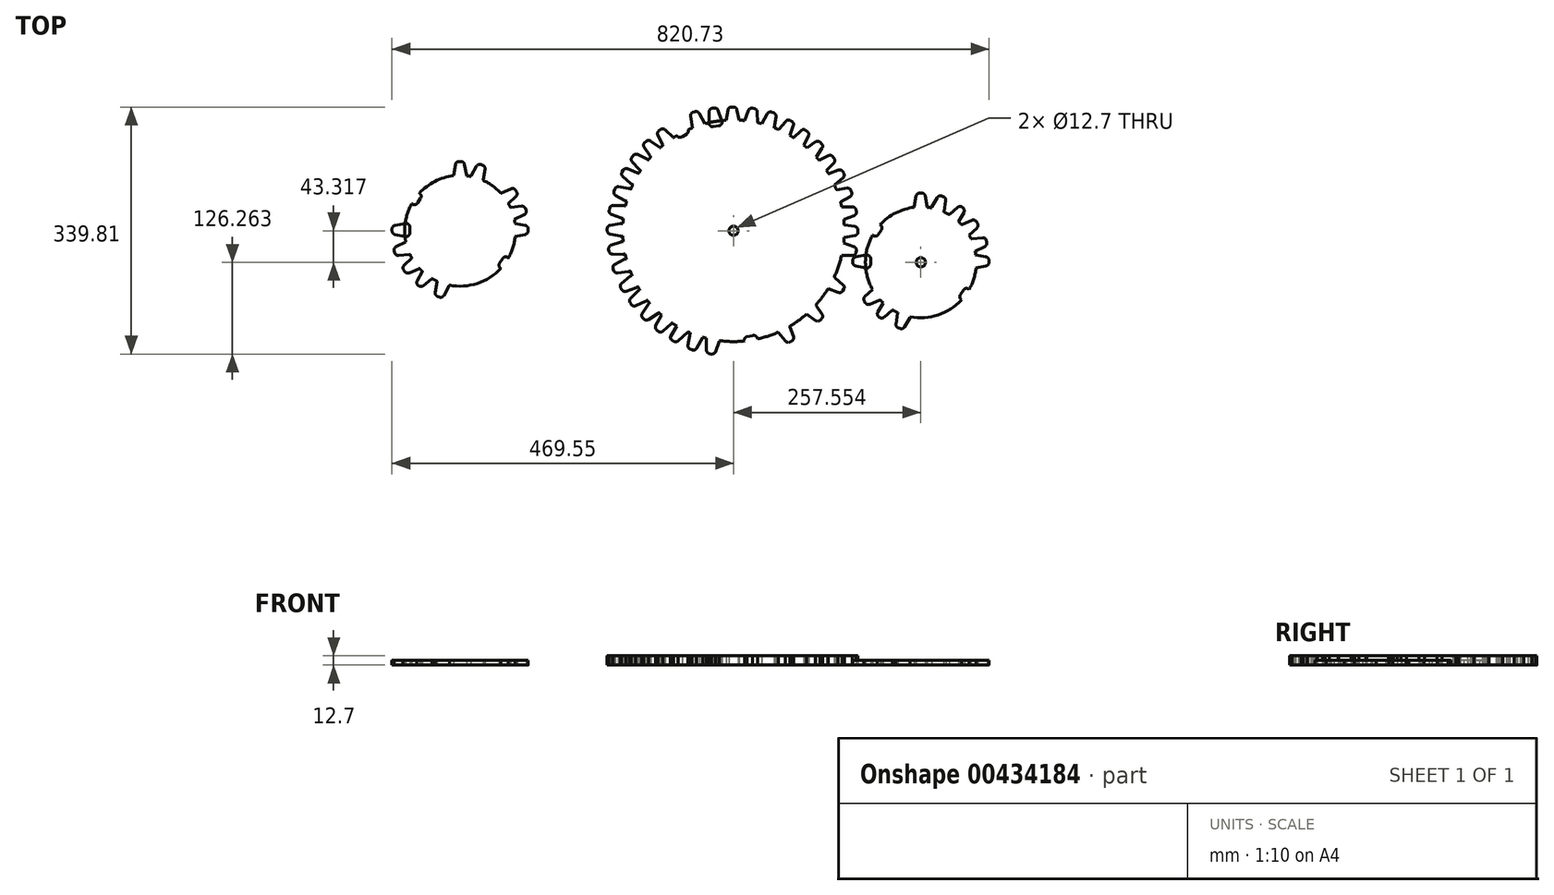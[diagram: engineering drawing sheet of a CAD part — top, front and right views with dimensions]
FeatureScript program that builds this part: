
annotation { "Feature Type Name" : "Feature", "Feature Type Description" : "" }
export const myFeature = defineFeature(function(context is Context, id is Id, definition is map)
    precondition{}
    {
        {
            var Q0;
            Q0=qCreatedBy(makeId("Top.planeOp"),FACE);
            var sketch = newSketch(context, id + "F0", { "sketchPlane" : qUnion([Q0])});
            skCircle(sketch, "E0", {"center": v(0, 0) * mm, "radius": 152.4 * mm});
            skCircle(sketch, "E1", {"center": v(0, 0) * mm, "radius": 6.35 * mm});
            skCircle(sketch, "E2", {"center": v(-375.92, 0) * mm, "radius": 76.2 * mm});
            skCircle(sketch, "E3", {"center": v(-375.92, 0) * mm, "radius": 6.35 * mm});
            skLineSegment(sketch, "E4", {"start": v(-2.72, 170.23) * mm, "end": v(-0.18, 170.23) * mm});
            skLineSegment(sketch, "E5", {"start": v(4.82, 166.07) * mm, "end": v(7.48, 151.67) * mm});
            skLineSegment(sketch, "E6", {"start": v(-7.73, 165.99) * mm, "end": v(-10.15, 151.52) * mm});
            skLineSegment(sketch, "E7", {"start": v(-5.1, 145.6) * mm, "end": v(2.53, 145.66) * mm});
            skPoint(sketch, "E8.visualSharp", {"position": v(-7.01, 170.23) * mm});
            skArc(sketch, "E8.filletArc", {"start": v(-2.72, 170.23) * mm, "mid": v(-6, 169.03) * mm, "end": v(-7.73, 165.99) * mm});
            skPoint(sketch, "E9.visualSharp", {"position": v(4.05, 170.23) * mm});
            skArc(sketch, "E9.filletArc", {"start": v(4.82, 166.07) * mm, "mid": v(3.07, 169.05) * mm, "end": v(-0.18, 170.23) * mm});
            skPoint(sketch, "E10.visualSharp", {"position": v(8.58, 145.71) * mm});
            skArc(sketch, "E10.filletArc", {"start": v(2.53, 145.66) * mm, "mid": v(6.4, 147.51) * mm, "end": v(7.48, 151.67) * mm});
            skPoint(sketch, "E11.visualSharp", {"position": v(-11.16, 145.55) * mm});
            skArc(sketch, "E11.filletArc", {"start": v(-10.15, 151.52) * mm, "mid": v(-9, 147.38) * mm, "end": v(-5.1, 145.6) * mm});
            skLineSegment(sketch, "E12", {"start": v(26.05, 168.6) * mm, "end": v(28.55, 168.15) * mm});
            skLineSegment(sketch, "E13", {"start": v(32.75, 163.19) * mm, "end": v(32.88, 147.84) * mm});
            skLineSegment(sketch, "E14", {"start": v(20.38, 165.29) * mm, "end": v(15.25, 150.8) * mm});
            skLineSegment(sketch, "E15", {"start": v(19.2, 144.1) * mm, "end": v(26.96, 142.79) * mm});
            skArc(sketch, "E16.filletArc", {"start": v(26.05, 168.6) * mm, "mid": v(22.61, 167.98) * mm, "end": v(20.38, 165.29) * mm});
            skArc(sketch, "E17.filletArc", {"start": v(32.75, 163.19) * mm, "mid": v(31.55, 166.43) * mm, "end": v(28.55, 168.15) * mm});
            skArc(sketch, "E18.filletArc", {"start": v(26.96, 142.79) * mm, "mid": v(31.1, 143.94) * mm, "end": v(32.88, 147.84) * mm});
            skArc(sketch, "E19.filletArc", {"start": v(15.25, 150.8) * mm, "mid": v(15.65, 146.53) * mm, "end": v(19.2, 144.1) * mm});
            skLineSegment(sketch, "E20", {"start": v(52.66, 163.16) * mm, "end": v(55.04, 162.3) * mm});
            skLineSegment(sketch, "E21", {"start": v(58.32, 156.68) * mm, "end": v(55.65, 140.78) * mm});
            skLineSegment(sketch, "E22", {"start": v(46.5, 160.9) * mm, "end": v(38.54, 146.85) * mm});
            skLineSegment(sketch, "E23", {"start": v(41.27, 139.56) * mm, "end": v(48.94, 136.83) * mm});
            skArc(sketch, "E24.filletArc", {"start": v(52.66, 163.16) * mm, "mid": v(49.16, 163.16) * mm, "end": v(46.5, 160.9) * mm});
            skArc(sketch, "E25.filletArc", {"start": v(58.32, 156.68) * mm, "mid": v(57.7, 160.08) * mm, "end": v(55.04, 162.3) * mm});
            skArc(sketch, "E26.filletArc", {"start": v(48.94, 136.83) * mm, "mid": v(53.21, 137.24) * mm, "end": v(55.65, 140.78) * mm});
            skArc(sketch, "E27.filletArc", {"start": v(38.54, 146.85) * mm, "mid": v(38.2, 142.57) * mm, "end": v(41.27, 139.56) * mm});
            skLineSegment(sketch, "E28", {"start": v(78, 151.7) * mm, "end": v(79.99, 150.55) * mm});
            skLineSegment(sketch, "E29", {"start": v(82.23, 144.45) * mm, "end": v(77.34, 130.64) * mm});
            skLineSegment(sketch, "E30", {"start": v(71.55, 150.52) * mm, "end": v(62.21, 139.2) * mm});
            skLineSegment(sketch, "E31", {"start": v(63.63, 131.56) * mm, "end": v(70.05, 127.92) * mm});
            skArc(sketch, "E32.filletArc", {"start": v(78, 151.7) * mm, "mid": v(74.56, 152.3) * mm, "end": v(71.55, 150.52) * mm});
            skArc(sketch, "E33.filletArc", {"start": v(82.23, 144.45) * mm, "mid": v(82.21, 147.9) * mm, "end": v(79.99, 150.55) * mm});
            skArc(sketch, "E34.filletArc", {"start": v(70.05, 127.92) * mm, "mid": v(74.33, 127.58) * mm, "end": v(77.34, 130.64) * mm});
            skArc(sketch, "E35.filletArc", {"start": v(62.21, 139.2) * mm, "mid": v(61.13, 135.05) * mm, "end": v(63.63, 131.56) * mm});
            skLineSegment(sketch, "E36", {"start": v(99.42, 138.15) * mm, "end": v(101.44, 136.6) * mm});
            skLineSegment(sketch, "E37", {"start": v(102.88, 130.27) * mm, "end": v(96.23, 117.22) * mm});
            skLineSegment(sketch, "E38", {"start": v(92.87, 137.83) * mm, "end": v(82.14, 127.83) * mm});
            skLineSegment(sketch, "E39", {"start": v(82.55, 120.05) * mm, "end": v(88.65, 115.46) * mm});
            skArc(sketch, "E40.filletArc", {"start": v(99.42, 138.15) * mm, "mid": v(96.09, 139.2) * mm, "end": v(92.87, 137.83) * mm});
            skArc(sketch, "E41.filletArc", {"start": v(102.88, 130.27) * mm, "mid": v(103.3, 133.7) * mm, "end": v(101.44, 136.6) * mm});
            skArc(sketch, "E42.filletArc", {"start": v(88.65, 115.46) * mm, "mid": v(92.85, 114.57) * mm, "end": v(96.23, 117.22) * mm});
            skArc(sketch, "E43.filletArc", {"start": v(82.14, 127.83) * mm, "mid": v(80.53, 123.84) * mm, "end": v(82.55, 120.05) * mm});
            skLineSegment(sketch, "E44", {"start": v(119.21, 121.66) * mm, "end": v(121, 119.87) * mm});
            skLineSegment(sketch, "E45", {"start": v(121.6, 113.4) * mm, "end": v(113.3, 101.33) * mm});
            skLineSegment(sketch, "E46", {"start": v(112.67, 122.2) * mm, "end": v(100.73, 113.7) * mm});
            skLineSegment(sketch, "E47", {"start": v(100.11, 105.94) * mm, "end": v(105.55, 100.58) * mm});
            skArc(sketch, "E48.filletArc", {"start": v(119.21, 121.66) * mm, "mid": v(116.04, 123.13) * mm, "end": v(112.67, 122.2) * mm});
            skArc(sketch, "E49.filletArc", {"start": v(121.6, 113.4) * mm, "mid": v(122.48, 116.74) * mm, "end": v(121, 119.87) * mm});
            skArc(sketch, "E50.filletArc", {"start": v(105.55, 100.58) * mm, "mid": v(109.6, 99.15) * mm, "end": v(113.3, 101.33) * mm});
            skArc(sketch, "E51.filletArc", {"start": v(100.73, 113.7) * mm, "mid": v(98.61, 109.96) * mm, "end": v(100.11, 105.94) * mm});
            skLineSegment(sketch, "E52", {"start": v(136.86, 101.65) * mm, "end": v(138.32, 99.57) * mm});
            skLineSegment(sketch, "E53", {"start": v(137.78, 93.1) * mm, "end": v(127.5, 82.65) * mm});
            skLineSegment(sketch, "E54", {"start": v(130.52, 103.32) * mm, "end": v(117.27, 97.01) * mm});
            skLineSegment(sketch, "E55", {"start": v(115.32, 89.48) * mm, "end": v(119.75, 83.26) * mm});
            skArc(sketch, "E56.filletArc", {"start": v(136.86, 101.65) * mm, "mid": v(134, 103.65) * mm, "end": v(130.52, 103.32) * mm});
            skArc(sketch, "E57.filletArc", {"start": v(137.78, 93.1) * mm, "mid": v(139.22, 96.23) * mm, "end": v(138.32, 99.57) * mm});
            skArc(sketch, "E58.filletArc", {"start": v(119.75, 83.26) * mm, "mid": v(123.49, 81.15) * mm, "end": v(127.5, 82.65) * mm});
            skArc(sketch, "E59.filletArc", {"start": v(117.27, 97.01) * mm, "mid": v(114.54, 93.7) * mm, "end": v(115.32, 89.48) * mm});
            skLineSegment(sketch, "E60", {"start": v(150.3, 81.3) * mm, "end": v(151.56, 79.1) * mm});
            skLineSegment(sketch, "E61", {"start": v(150.46, 72.7) * mm, "end": v(139.32, 63.18) * mm});
            skLineSegment(sketch, "E62", {"start": v(144.12, 83.51) * mm, "end": v(130.37, 78.38) * mm});
            skLineSegment(sketch, "E63", {"start": v(127.77, 71.05) * mm, "end": v(131.64, 64.47) * mm});
            skArc(sketch, "E64.filletArc", {"start": v(150.3, 81.3) * mm, "mid": v(147.61, 83.54) * mm, "end": v(144.12, 83.51) * mm});
            skArc(sketch, "E65.filletArc", {"start": v(150.46, 72.7) * mm, "mid": v(152.17, 75.7) * mm, "end": v(151.56, 79.1) * mm});
            skArc(sketch, "E66.filletArc", {"start": v(131.64, 64.47) * mm, "mid": v(135.18, 62.04) * mm, "end": v(139.32, 63.18) * mm});
            skArc(sketch, "E67.filletArc", {"start": v(130.37, 78.38) * mm, "mid": v(127.36, 75.32) * mm, "end": v(127.77, 71.05) * mm});
            skLineSegment(sketch, "E68", {"start": v(161.65, 55.18) * mm, "end": v(162.43, 52.77) * mm});
            skLineSegment(sketch, "E69", {"start": v(160.02, 46.73) * mm, "end": v(147.14, 39.75) * mm});
            skLineSegment(sketch, "E70", {"start": v(156.07, 58.64) * mm, "end": v(141.56, 56.48) * mm});
            skLineSegment(sketch, "E71", {"start": v(137.48, 49.85) * mm, "end": v(139.9, 42.61) * mm});
            skArc(sketch, "E72.filletArc", {"start": v(161.65, 55.18) * mm, "mid": v(159.49, 57.93) * mm, "end": v(156.07, 58.64) * mm});
            skArc(sketch, "E73.filletArc", {"start": v(160.02, 46.73) * mm, "mid": v(162.31, 49.31) * mm, "end": v(162.43, 52.77) * mm});
            skArc(sketch, "E74.filletArc", {"start": v(139.9, 42.61) * mm, "mid": v(142.85, 39.5) * mm, "end": v(147.14, 39.75) * mm});
            skArc(sketch, "E75.filletArc", {"start": v(141.56, 56.48) * mm, "mid": v(137.97, 54.12) * mm, "end": v(137.48, 49.85) * mm});
            skLineSegment(sketch, "E76", {"start": v(168.33, 28.75) * mm, "end": v(168.77, 26.25) * mm});
            skLineSegment(sketch, "E77", {"start": v(165.55, 20.6) * mm, "end": v(151.82, 15.48) * mm});
            skLineSegment(sketch, "E78", {"start": v(163.29, 32.95) * mm, "end": v(148.62, 32.83) * mm});
            skLineSegment(sketch, "E79", {"start": v(143.66, 26.82) * mm, "end": v(145.05, 19.32) * mm});
            skArc(sketch, "E80.filletArc", {"start": v(168.33, 28.75) * mm, "mid": v(166.58, 31.77) * mm, "end": v(163.29, 32.95) * mm});
            skArc(sketch, "E81.filletArc", {"start": v(165.55, 20.6) * mm, "mid": v(168.18, 22.85) * mm, "end": v(168.77, 26.25) * mm});
            skArc(sketch, "E82.filletArc", {"start": v(145.05, 19.32) * mm, "mid": v(147.54, 15.82) * mm, "end": v(151.82, 15.48) * mm});
            skArc(sketch, "E83.filletArc", {"start": v(148.62, 32.83) * mm, "mid": v(144.74, 30.98) * mm, "end": v(143.66, 26.82) * mm});
            skLineSegment(sketch, "E84", {"start": v(171.1, 0.88) * mm, "end": v(171.1, -1.66) * mm});
            skLineSegment(sketch, "E85", {"start": v(166.93, -6.65) * mm, "end": v(152.53, -9.31) * mm});
            skLineSegment(sketch, "E86", {"start": v(166.85, 5.9) * mm, "end": v(152.38, 8.32) * mm});
            skLineSegment(sketch, "E87", {"start": v(146.46, 3.27) * mm, "end": v(146.53, -4.36) * mm});
            skArc(sketch, "E88.filletArc", {"start": v(171.1, 0.88) * mm, "mid": v(169.89, 4.17) * mm, "end": v(166.85, 5.9) * mm});
            skArc(sketch, "E89.filletArc", {"start": v(166.93, -6.65) * mm, "mid": v(169.92, -4.9) * mm, "end": v(171.1, -1.66) * mm});
            skArc(sketch, "E90.filletArc", {"start": v(146.53, -4.36) * mm, "mid": v(148.37, -8.24) * mm, "end": v(152.53, -9.31) * mm});
            skArc(sketch, "E91.filletArc", {"start": v(152.38, 8.32) * mm, "mid": v(148.25, 7.18) * mm, "end": v(146.46, 3.27) * mm});
            skArc(sketch, "E92.MirrorCS", {"start": v(32.75, -164.43) * mm, "mid": v(31.55, -167.65) * mm, "end": v(28.57, -169.36) * mm});
            skLineSegment(sketch, "E93.MirrorCS", {"start": v(26.07, -169.8) * mm, "end": v(28.57, -169.36) * mm});
            skArc(sketch, "E94.MirrorCS", {"start": v(81.8, -128.72) * mm, "mid": v(80.51, -125.06) * mm, "end": v(82.17, -121.56) * mm});
            skArc(sketch, "E95.MirrorCS", {"start": v(15.04, -151.45) * mm, "mid": v(15.62, -147.73) * mm, "end": v(18.6, -145.4) * mm});
            skLineSegment(sketch, "E96.MirrorCS", {"start": v(18.6, -145.4) * mm, "end": v(26.36, -144.1) * mm});
            skArc(sketch, "E97.MirrorCS", {"start": v(26.36, -144.1) * mm, "mid": v(30.63, -144.76) * mm, "end": v(32.88, -148.45) * mm});
            skLineSegment(sketch, "E98.MirrorCS", {"start": v(82.17, -121.56) * mm, "end": v(88.88, -116.5) * mm});
            skLineSegment(sketch, "E99.MirrorCS", {"start": v(168.32, -30.06) * mm, "end": v(168.87, -26.9) * mm});
            skArc(sketch, "E100.MirrorCS", {"start": v(99.04, -139.66) * mm, "mid": v(95.6, -140.39) * mm, "end": v(92.52, -138.72) * mm});
            skLineSegment(sketch, "E101.MirrorCS", {"start": v(63.17, -133.03) * mm, "end": v(70.24, -129.03) * mm});
            skArc(sketch, "E102.MirrorCS", {"start": v(165, -21.62) * mm, "mid": v(167.89, -23.55) * mm, "end": v(168.87, -26.9) * mm});
            skArc(sketch, "E103.MirrorCS", {"start": v(141.38, -57.68) * mm, "mid": v(137.97, -55.34) * mm, "end": v(137.43, -51.23) * mm});
            skArc(sketch, "E104.MirrorCS", {"start": v(4.8, -167.37) * mm, "mid": v(3, -170.32) * mm, "end": v(-0.26, -171.44) * mm});
            skArc(sketch, "E105.MirrorCS", {"start": v(26.07, -169.8) * mm, "mid": v(22.63, -169.2) * mm, "end": v(20.39, -166.52) * mm});
            skArc(sketch, "E106.MirrorCS", {"start": v(131.88, -65.27) * mm, "mid": v(135.65, -63.18) * mm, "end": v(139.68, -64.71) * mm});
            skArc(sketch, "E107.MirrorCS", {"start": v(168.32, -30.06) * mm, "mid": v(166.5, -33.05) * mm, "end": v(163.2, -34.16) * mm});
            skArc(sketch, "E108.MirrorCS", {"start": v(-10.25, -152.13) * mm, "mid": v(-9.04, -148.58) * mm, "end": v(-5.72, -146.81) * mm});
            skArc(sketch, "E109.MirrorCS", {"start": v(70.24, -129.03) * mm, "mid": v(74.54, -128.88) * mm, "end": v(77.41, -132.07) * mm});
            skLineSegment(sketch, "E110.MirrorCS", {"start": v(118.91, -123.18) * mm, "end": v(121.27, -120.82) * mm});
            skLineSegment(sketch, "E111.MirrorCS", {"start": v(-3.33, -171.44) * mm, "end": v(-0.26, -171.44) * mm});
            skArc(sketch, "E112.MirrorCS", {"start": v(-3.33, -171.44) * mm, "mid": v(-6.47, -169.85) * mm, "end": v(-7.83, -166.6) * mm});
            skArc(sketch, "E113.MirrorCS", {"start": v(1.95, -146.88) * mm, "mid": v(6.03, -148.28) * mm, "end": v(7.59, -152.31) * mm});
            skLineSegment(sketch, "E114.MirrorCS", {"start": v(-5.72, -146.81) * mm, "end": v(1.95, -146.88) * mm});
            skArc(sketch, "E115.MirrorCS", {"start": v(118.91, -123.18) * mm, "mid": v(115.62, -124.38) * mm, "end": v(112.33, -123.18) * mm});
            skArc(sketch, "E116.MirrorCS", {"start": v(120, -84.12) * mm, "mid": v(123.93, -82.33) * mm, "end": v(127.82, -84.18) * mm});
            skArc(sketch, "E117.MirrorCS", {"start": v(116.97, -98.08) * mm, "mid": v(114.53, -94.92) * mm, "end": v(115.13, -90.97) * mm});
            skArc(sketch, "E118.MirrorCS", {"start": v(138.1, -94.63) * mm, "mid": v(139.24, -97.45) * mm, "end": v(138.58, -100.42) * mm});
            skArc(sketch, "E119.MirrorCS", {"start": v(58.34, -158.02) * mm, "mid": v(57.7, -161.3) * mm, "end": v(55.16, -163.47) * mm});
            skLineSegment(sketch, "E120.MirrorCS", {"start": v(99.81, -107.45) * mm, "end": v(105.81, -101.55) * mm});
            skLineSegment(sketch, "E121.MirrorCS", {"start": v(121.81, -114.91) * mm, "end": v(113.5, -102.84) * mm});
            skLineSegment(sketch, "E122.MirrorCS", {"start": v(165, -21.62) * mm, "end": v(151.28, -16.5) * mm});
            skLineSegment(sketch, "E123.MirrorCS", {"start": v(115.13, -90.97) * mm, "end": v(120, -84.12) * mm});
            skLineSegment(sketch, "E124.MirrorCS", {"start": v(40.73, -140.96) * mm, "end": v(48.36, -138.26) * mm});
            skArc(sketch, "E125.MirrorCS", {"start": v(48.36, -138.26) * mm, "mid": v(52.68, -138.15) * mm, "end": v(55.55, -141.4) * mm});
            skArc(sketch, "E126.MirrorCS", {"start": v(88.88, -116.5) * mm, "mid": v(93.14, -115.86) * mm, "end": v(96.36, -118.7) * mm});
            skArc(sketch, "E127.MirrorCS", {"start": v(140.07, -43.3) * mm, "mid": v(143.36, -40.51) * mm, "end": v(147.62, -41.23) * mm});
            skArc(sketch, "E128.MirrorCS", {"start": v(52.12, -164.58) * mm, "mid": v(48.63, -164.17) * mm, "end": v(46.22, -161.61) * mm});
            skLineSegment(sketch, "E129.MirrorCS", {"start": v(150.15, -82.77) * mm, "end": v(151.8, -79.9) * mm});
            skLineSegment(sketch, "E130.MirrorCS", {"start": v(77.55, -153.17) * mm, "end": v(80.18, -151.65) * mm});
            skLineSegment(sketch, "E131.MirrorCS", {"start": v(92.52, -138.72) * mm, "end": v(81.8, -128.72) * mm});
            skLineSegment(sketch, "E132.MirrorCS", {"start": v(71.21, -151.34) * mm, "end": v(61.88, -140.02) * mm});
            skArc(sketch, "E133.MirrorCS", {"start": v(38.26, -147.57) * mm, "mid": v(38.17, -143.77) * mm, "end": v(40.73, -140.96) * mm});
            skArc(sketch, "E134.MirrorCS", {"start": v(159.53, -47.69) * mm, "mid": v(162.1, -50.02) * mm, "end": v(162.6, -53.46) * mm});
            skArc(sketch, "E135.MirrorCS", {"start": v(103.01, -131.75) * mm, "mid": v(103.31, -134.92) * mm, "end": v(101.68, -137.64) * mm});
            skLineSegment(sketch, "E136.MirrorCS", {"start": v(20.39, -166.52) * mm, "end": v(15.04, -151.45) * mm});
            skLineSegment(sketch, "E137.MirrorCS", {"start": v(137.43, -51.23) * mm, "end": v(140.07, -43.3) * mm});
            skLineSegment(sketch, "E138.MirrorCS", {"start": v(143.65, -28.13) * mm, "end": v(145.16, -19.96) * mm});
            skArc(sketch, "E139.MirrorCS", {"start": v(100.38, -114.67) * mm, "mid": v(98.6, -111.18) * mm, "end": v(99.81, -107.45) * mm});
            skLineSegment(sketch, "E140.MirrorCS", {"start": v(130.21, -104.39) * mm, "end": v(116.97, -98.08) * mm});
            skArc(sketch, "E141.MirrorCS", {"start": v(145.16, -19.96) * mm, "mid": v(147.53, -17.01) * mm, "end": v(151.28, -16.5) * mm});
            skArc(sketch, "E142.MirrorCS", {"start": v(105.81, -101.55) * mm, "mid": v(109.96, -100.4) * mm, "end": v(113.5, -102.84) * mm});
            skArc(sketch, "E143.MirrorCS", {"start": v(161.6, -56.57) * mm, "mid": v(159.34, -59.24) * mm, "end": v(155.9, -59.83) * mm});
            skArc(sketch, "E144.MirrorCS", {"start": v(121.81, -114.91) * mm, "mid": v(122.49, -117.96) * mm, "end": v(121.27, -120.82) * mm});
            skLineSegment(sketch, "E145.MirrorCS", {"start": v(138.1, -94.63) * mm, "end": v(127.82, -84.18) * mm});
            skArc(sketch, "E146.MirrorCS", {"start": v(82.31, -145.88) * mm, "mid": v(82.22, -149.12) * mm, "end": v(80.18, -151.65) * mm});
            skLineSegment(sketch, "E147.MirrorCS", {"start": v(161.6, -56.57) * mm, "end": v(162.6, -53.46) * mm});
            skArc(sketch, "E148.MirrorCS", {"start": v(130.1, -79.5) * mm, "mid": v(127.35, -76.54) * mm, "end": v(127.62, -72.52) * mm});
            skArc(sketch, "E149.MirrorCS", {"start": v(136.67, -103.14) * mm, "mid": v(133.67, -104.95) * mm, "end": v(130.21, -104.39) * mm});
            skLineSegment(sketch, "E150.MirrorCS", {"start": v(159.53, -47.69) * mm, "end": v(147.62, -41.23) * mm});
            skLineSegment(sketch, "E151.MirrorCS", {"start": v(155.9, -59.83) * mm, "end": v(141.38, -57.68) * mm});
            skLineSegment(sketch, "E152.MirrorCS", {"start": v(103.01, -131.75) * mm, "end": v(96.36, -118.7) * mm});
            skLineSegment(sketch, "E153.MirrorCS", {"start": v(143.84, -84.63) * mm, "end": v(130.1, -79.5) * mm});
            skLineSegment(sketch, "E154.MirrorCS", {"start": v(136.67, -103.14) * mm, "end": v(138.58, -100.42) * mm});
            skLineSegment(sketch, "E155.MirrorCS", {"start": v(150.83, -74.22) * mm, "end": v(139.68, -64.71) * mm});
            skArc(sketch, "E156.MirrorCS", {"start": v(150.83, -74.22) * mm, "mid": v(152.2, -76.9) * mm, "end": v(151.8, -79.9) * mm});
            skLineSegment(sketch, "E157.MirrorCS", {"start": v(82.31, -145.88) * mm, "end": v(77.41, -132.07) * mm});
            skLineSegment(sketch, "E158.MirrorCS", {"start": v(52.12, -164.58) * mm, "end": v(55.16, -163.47) * mm});
            skArc(sketch, "E159.MirrorCS", {"start": v(61.88, -140.02) * mm, "mid": v(61.1, -136.26) * mm, "end": v(63.17, -133.03) * mm});
            skLineSegment(sketch, "E160.MirrorCS", {"start": v(99.04, -139.66) * mm, "end": v(101.68, -137.64) * mm});
            skLineSegment(sketch, "E161.MirrorCS", {"start": v(112.33, -123.18) * mm, "end": v(100.38, -114.67) * mm});
            skArc(sketch, "E162.MirrorCS", {"start": v(77.55, -153.17) * mm, "mid": v(74.05, -153.41) * mm, "end": v(71.21, -151.34) * mm});
            skArc(sketch, "E163.MirrorCS", {"start": v(150.15, -82.77) * mm, "mid": v(147.33, -84.85) * mm, "end": v(143.84, -84.63) * mm});
            skLineSegment(sketch, "E164.MirrorCS", {"start": v(127.62, -72.52) * mm, "end": v(131.88, -65.27) * mm});
            skArc(sketch, "E165.MirrorCS", {"start": v(148.53, -34.04) * mm, "mid": v(144.74, -32.2) * mm, "end": v(143.65, -28.13) * mm});
            skLineSegment(sketch, "E166.MirrorCS", {"start": v(163.2, -34.16) * mm, "end": v(148.53, -34.04) * mm});
            skLineSegment(sketch, "E167.MirrorCS", {"start": v(46.22, -161.61) * mm, "end": v(38.26, -147.57) * mm});
            skLineSegment(sketch, "E168.MirrorCS", {"start": v(58.34, -158.02) * mm, "end": v(55.55, -141.4) * mm});
            skLineSegment(sketch, "E169.MirrorCS", {"start": v(4.8, -167.37) * mm, "end": v(7.59, -152.31) * mm});
            skLineSegment(sketch, "E170.MirrorCS", {"start": v(32.75, -164.43) * mm, "end": v(32.88, -148.45) * mm});
            skPoint(sketch, "E171.MirrorP", {"position": v(-11.16, -146.77) * mm});
            skPoint(sketch, "E172.MirrorP", {"position": v(8.58, -146.93) * mm});
            skLineSegment(sketch, "E173.MirrorCS", {"start": v(-7.83, -166.6) * mm, "end": v(-10.25, -152.13) * mm});
            skLineSegment(sketch, "E174.MirrorCS", {"start": v(-173.6, 3.46) * mm, "end": v(-173.64, 0.11) * mm});
            skArc(sketch, "E175.MirrorCS", {"start": v(-82.62, -151.8) * mm, "mid": v(-79.23, -152.7) * mm, "end": v(-76.06, -151.2) * mm});
            skArc(sketch, "E176.MirrorCS", {"start": v(-103.9, -137.94) * mm, "mid": v(-100.67, -139.3) * mm, "end": v(-97.32, -138.26) * mm});
            skArc(sketch, "E177.MirrorCS", {"start": v(-86.57, -145.06) * mm, "mid": v(-86.46, -148.16) * mm, "end": v(-84.59, -150.63) * mm});
            skLineSegment(sketch, "E178.MirrorCS", {"start": v(-163.37, 57.56) * mm, "end": v(-164.47, 54.28) * mm});
            skArc(sketch, "E179.MirrorCS", {"start": v(-107.12, -130.68) * mm, "mid": v(-107.4, -133.72) * mm, "end": v(-105.9, -136.37) * mm});
            skLineSegment(sketch, "E180.MirrorCS", {"start": v(-137.97, 103.58) * mm, "end": v(-140, 100.75) * mm});
            skArc(sketch, "E181.MirrorCS", {"start": v(-173.6, 3.46) * mm, "mid": v(-172.4, 6.14) * mm, "end": v(-169.91, 7.72) * mm});
            skArc(sketch, "E182.MirrorCS", {"start": v(-147.42, 20.7) * mm, "mid": v(-150.15, 17.38) * mm, "end": v(-154.45, 17.34) * mm});
            skLineSegment(sketch, "E183.MirrorCS", {"start": v(-103.9, -137.94) * mm, "end": v(-105.9, -136.37) * mm});
            skArc(sketch, "E184.MirrorCS", {"start": v(-139.6, 95.03) * mm, "mid": v(-140.68, 97.83) * mm, "end": v(-140, 100.75) * mm});
            skArc(sketch, "E185.MirrorCS", {"start": v(-149.1, -2.87) * mm, "mid": v(-151.15, -6.65) * mm, "end": v(-155.36, -7.52) * mm});
            skLineSegment(sketch, "E186.MirrorCS", {"start": v(-78.61, 152.7) * mm, "end": v(-81.33, 151.17) * mm});
            skArc(sketch, "E187.MirrorCS", {"start": v(-163.37, 57.56) * mm, "mid": v(-161.37, 59.8) * mm, "end": v(-158.47, 60.52) * mm});
            skArc(sketch, "E188.MirrorCS", {"start": v(-137.97, 103.58) * mm, "mid": v(-135.35, 105.2) * mm, "end": v(-132.27, 105.01) * mm});
            skArc(sketch, "E189.MirrorCS", {"start": v(-78.61, 152.7) * mm, "mid": v(-75.14, 153.1) * mm, "end": v(-72.22, 151.17) * mm});
            skLineSegment(sketch, "E190.MirrorCS", {"start": v(-151.65, 83.43) * mm, "end": v(-153.42, 80.44) * mm});
            skArc(sketch, "E191.MirrorCS", {"start": v(-83.31, 145.96) * mm, "mid": v(-83.1, 148.86) * mm, "end": v(-81.33, 151.17) * mm});
            skLineSegment(sketch, "E192.MirrorCS", {"start": v(-82.62, -151.8) * mm, "end": v(-84.59, -150.63) * mm});
            skArc(sketch, "E193.MirrorCS", {"start": v(-27.85, 143.1) * mm, "mid": v(-31.98, 144.3) * mm, "end": v(-33.72, 148.22) * mm});
            skArc(sketch, "E194.MirrorCS", {"start": v(-169.74, -4.69) * mm, "mid": v(-172.5, -2.95) * mm, "end": v(-173.64, 0.11) * mm});
            skLineSegment(sketch, "E195.MirrorCS", {"start": v(-123.15, 115.25) * mm, "end": v(-114.98, 103.09) * mm});
            skArc(sketch, "E196.MirrorCS", {"start": v(-152.5, 74.73) * mm, "mid": v(-153.85, 77.44) * mm, "end": v(-153.42, 80.44) * mm});
            skLineSegment(sketch, "E197.MirrorCS", {"start": v(-83.31, 145.96) * mm, "end": v(-78.3, 131.32) * mm});
            skArc(sketch, "E198.MirrorCS", {"start": v(-101.67, 114.64) * mm, "mid": v(-99.87, 111.1) * mm, "end": v(-101.18, 107.34) * mm});
            skArc(sketch, "E199.MirrorCS", {"start": v(-132.45, 80.06) * mm, "mid": v(-129.19, 77.24) * mm, "end": v(-129.24, 72.93) * mm});
            skArc(sketch, "E200.MirrorCS", {"start": v(-118.3, 98.17) * mm, "mid": v(-115.98, 95.02) * mm, "end": v(-116.57, 91.16) * mm});
            skLineSegment(sketch, "E201.MirrorCS", {"start": v(-116.57, 91.16) * mm, "end": v(-121.62, 84.24) * mm});
            skArc(sketch, "E202.MirrorCS", {"start": v(-62.7, -157.5) * mm, "mid": v(-62.08, -160.62) * mm, "end": v(-59.72, -162.75) * mm});
            skLineSegment(sketch, "E203.MirrorCS", {"start": v(-148.94, 5.56) * mm, "end": v(-149.1, -2.87) * mm});
            skLineSegment(sketch, "E204.MirrorCS", {"start": v(-42.1, 140.07) * mm, "end": v(-49.8, 137.44) * mm});
            skLineSegment(sketch, "E205.MirrorCS", {"start": v(-47.14, 161.32) * mm, "end": v(-39.35, 147.2) * mm});
            skArc(sketch, "E206.MirrorCS", {"start": v(-107.33, 101.42) * mm, "mid": v(-111.55, 100.47) * mm, "end": v(-114.98, 103.09) * mm});
            skLineSegment(sketch, "E207.MirrorCS", {"start": v(-53.21, 163.8) * mm, "end": v(-56.3, 162.72) * mm});
            skArc(sketch, "E208.MirrorCS", {"start": v(-141.78, -93.1) * mm, "mid": v(-142.9, -95.83) * mm, "end": v(-142.31, -98.73) * mm});
            skLineSegment(sketch, "E209.MirrorCS", {"start": v(-139.6, 95.03) * mm, "end": v(-129.44, 84.47) * mm});
            skLineSegment(sketch, "E210.MirrorCS", {"start": v(-141.78, -93.1) * mm, "end": v(-130.74, -82.13) * mm});
            skArc(sketch, "E211.MirrorCS", {"start": v(-83, 128.57) * mm, "mid": v(-81.64, 124.77) * mm, "end": v(-83.48, 121.18) * mm});
            skArc(sketch, "E212.MirrorCS", {"start": v(-53.6, -137.27) * mm, "mid": v(-57.35, -137.8) * mm, "end": v(-59.7, -140.76) * mm});
            skLineSegment(sketch, "E213.MirrorCS", {"start": v(-93.61, 138.7) * mm, "end": v(-83, 128.57) * mm});
            skLineSegment(sketch, "E214.MirrorCS", {"start": v(-132.27, 105.01) * mm, "end": v(-118.3, 98.17) * mm});
            skArc(sketch, "E215.MirrorCS", {"start": v(-120.77, -96.8) * mm, "mid": v(-118.15, -93.59) * mm, "end": v(-118.79, -89.5) * mm});
            skArc(sketch, "E216.MirrorCS", {"start": v(-39.35, 147.2) * mm, "mid": v(-39.1, 143) * mm, "end": v(-42.1, 140.07) * mm});
            skLineSegment(sketch, "E217.MirrorCS", {"start": v(-118.79, -89.5) * mm, "end": v(-123.04, -83.4) * mm});
            skArc(sketch, "E218.MirrorCS", {"start": v(-104.35, -113.58) * mm, "mid": v(-102.4, -110.03) * mm, "end": v(-103.67, -106.18) * mm});
            skArc(sketch, "E219.MirrorCS", {"start": v(-123.15, 115.25) * mm, "mid": v(-123.7, 118.15) * mm, "end": v(-122.57, 120.87) * mm});
            skArc(sketch, "E220.MirrorCS", {"start": v(-123.04, -83.4) * mm, "mid": v(-126.6, -80.96) * mm, "end": v(-130.74, -82.13) * mm});
            skArc(sketch, "E221.MirrorCS", {"start": v(-140.88, -100.82) * mm, "mid": v(-138.26, -103.16) * mm, "end": v(-134.74, -103.25) * mm});
            skArc(sketch, "E222.MirrorCS", {"start": v(-147.92, -18.26) * mm, "mid": v(-150.8, -15.03) * mm, "end": v(-155.12, -15.16) * mm});
            skArc(sketch, "E223.MirrorCS", {"start": v(-133.67, 65.59) * mm, "mid": v(-137.46, 63.52) * mm, "end": v(-141.47, 65.1) * mm});
            skArc(sketch, "E224.MirrorCS", {"start": v(-143.98, 58.2) * mm, "mid": v(-140.17, 56.17) * mm, "end": v(-139.27, 51.95) * mm});
            skLineSegment(sketch, "E225.MirrorCS", {"start": v(-59.16, 157.96) * mm, "end": v(-56.56, 141.34) * mm});
            skLineSegment(sketch, "E226.MirrorCS", {"start": v(-139.27, 51.95) * mm, "end": v(-142.06, 43.87) * mm});
            skLineSegment(sketch, "E227.MirrorCS", {"start": v(-83.48, 121.18) * mm, "end": v(-90.33, 116.14) * mm});
            skArc(sketch, "E228.MirrorCS", {"start": v(-16.06, 150.98) * mm, "mid": v(-16.52, 146.71) * mm, "end": v(-20.07, 144.32) * mm});
            skLineSegment(sketch, "E229.MirrorCS", {"start": v(-129.24, 72.93) * mm, "end": v(-133.67, 65.59) * mm});
            skArc(sketch, "E230.MirrorCS", {"start": v(-120.1, 123.29) * mm, "mid": v(-116.8, 124.5) * mm, "end": v(-113.51, 123.29) * mm});
            skArc(sketch, "E231.MirrorCS", {"start": v(-151.65, 83.43) * mm, "mid": v(-149.2, 85.25) * mm, "end": v(-146.14, 85.34) * mm});
            skArc(sketch, "E232.MirrorCS", {"start": v(-57.35, -163.65) * mm, "mid": v(-53.86, -163.88) * mm, "end": v(-51.04, -161.8) * mm});
            skLineSegment(sketch, "E233.MirrorCS", {"start": v(-120.1, 123.29) * mm, "end": v(-122.57, 120.87) * mm});
            skArc(sketch, "E234.MirrorCS", {"start": v(-155.42, 9.98) * mm, "mid": v(-151.15, 9.28) * mm, "end": v(-148.94, 5.56) * mm});
            skLineSegment(sketch, "E235.MirrorCS", {"start": v(-72.22, 151.17) * mm, "end": v(-62.52, 139.03) * mm});
            skLineSegment(sketch, "E236.MirrorCS", {"start": v(-27.26, 168.8) * mm, "end": v(-29.77, 168.38) * mm});
            skLineSegment(sketch, "E237.MirrorCS", {"start": v(-168.12, 22.62) * mm, "end": v(-154.45, 17.34) * mm});
            skArc(sketch, "E238.MirrorCS", {"start": v(-142.06, 43.87) * mm, "mid": v(-145.28, 41) * mm, "end": v(-149.54, 41.63) * mm});
            skArc(sketch, "E239.MirrorCS", {"start": v(-59.16, 157.96) * mm, "mid": v(-58.43, 160.76) * mm, "end": v(-56.3, 162.72) * mm});
            skLineSegment(sketch, "E240.MirrorCS", {"start": v(-140.88, -100.82) * mm, "end": v(-142.31, -98.73) * mm});
            skArc(sketch, "E241.MirrorCS", {"start": v(-37.17, -164.2) * mm, "mid": v(-36, -167.26) * mm, "end": v(-33.22, -168.98) * mm});
            skArc(sketch, "E242.MirrorCS", {"start": v(-170.42, 31.26) * mm, "mid": v(-168.76, 33.72) * mm, "end": v(-166.02, 34.84) * mm});
            skArc(sketch, "E243.MirrorCS", {"start": v(-33.41, 164.17) * mm, "mid": v(-32.21, 166.82) * mm, "end": v(-29.77, 168.38) * mm});
            skLineSegment(sketch, "E244.MirrorCS", {"start": v(-33.41, 164.17) * mm, "end": v(-33.72, 148.22) * mm});
            skLineSegment(sketch, "E245.MirrorCS", {"start": v(-145.77, 29.05) * mm, "end": v(-147.42, 20.7) * mm});
            skArc(sketch, "E246.MirrorCS", {"start": v(-134.76, -64.45) * mm, "mid": v(-138.11, -61.75) * mm, "end": v(-142.33, -62.58) * mm});
            skArc(sketch, "E247.MirrorCS", {"start": v(-100.14, 139.47) * mm, "mid": v(-96.73, 140.28) * mm, "end": v(-93.61, 138.7) * mm});
            skLineSegment(sketch, "E248.MirrorCS", {"start": v(-30.72, -169.45) * mm, "end": v(-33.22, -168.98) * mm});
            skArc(sketch, "E249.MirrorCS", {"start": v(-168.12, 22.62) * mm, "mid": v(-170.45, 24.78) * mm, "end": v(-171.05, 27.9) * mm});
            skLineSegment(sketch, "E250.MirrorCS", {"start": v(-101.18, 107.34) * mm, "end": v(-107.33, 101.42) * mm});
            skLineSegment(sketch, "E251.MirrorCS", {"start": v(-166.02, 34.84) * mm, "end": v(-151.35, 34.55) * mm});
            skLineSegment(sketch, "E252.MirrorCS", {"start": v(-170.42, 31.26) * mm, "end": v(-171.05, 27.9) * mm});
            skArc(sketch, "E253.MirrorCS", {"start": v(-53.21, 163.8) * mm, "mid": v(-49.72, 163.68) * mm, "end": v(-47.14, 161.32) * mm});
            skLineSegment(sketch, "E254.MirrorCS", {"start": v(-57.35, -163.65) * mm, "end": v(-59.72, -162.75) * mm});
            skArc(sketch, "E255.MirrorCS", {"start": v(-151.35, 34.55) * mm, "mid": v(-147.28, 33.1) * mm, "end": v(-145.77, 29.05) * mm});
            skArc(sketch, "E256.MirrorCS", {"start": v(-49.8, 137.44) * mm, "mid": v(-54.06, 137.79) * mm, "end": v(-56.55, 141.26) * mm});
            skArc(sketch, "E257.MirrorCS", {"start": v(-30.72, -169.45) * mm, "mid": v(-27.26, -169) * mm, "end": v(-24.9, -166.43) * mm});
            skLineSegment(sketch, "E258.MirrorCS", {"start": v(-20.07, 144.32) * mm, "end": v(-27.85, 143.1) * mm});
            skArc(sketch, "E259.MirrorCS", {"start": v(-121.62, 84.24) * mm, "mid": v(-125.59, 82.53) * mm, "end": v(-129.44, 84.47) * mm});
            skLineSegment(sketch, "E260.MirrorCS", {"start": v(-146.14, 85.34) * mm, "end": v(-132.45, 80.06) * mm});
            skLineSegment(sketch, "E261.MirrorCS", {"start": v(-113.51, 123.29) * mm, "end": v(-101.67, 114.64) * mm});
            skArc(sketch, "E262.MirrorCS", {"start": v(-90.33, 116.14) * mm, "mid": v(-94.64, 115.78) * mm, "end": v(-97.68, 118.85) * mm});
            skLineSegment(sketch, "E263.MirrorCS", {"start": v(-169.91, 7.72) * mm, "end": v(-155.42, 9.98) * mm});
            skLineSegment(sketch, "E264.MirrorCS", {"start": v(-169.74, -4.69) * mm, "end": v(-155.36, -7.52) * mm});
            skArc(sketch, "E265.MirrorCS", {"start": v(-151.62, -32.33) * mm, "mid": v(-147.7, -30.6) * mm, "end": v(-146.5, -26.47) * mm});
            skLineSegment(sketch, "E266.MirrorCS", {"start": v(-100.14, 139.47) * mm, "end": v(-102.88, 137.42) * mm});
            skLineSegment(sketch, "E267.MirrorCS", {"start": v(-164.82, -54.53) * mm, "end": v(-165.75, -51.53) * mm});
            skArc(sketch, "E268.MirrorCS", {"start": v(-70.7, -129.43) * mm, "mid": v(-74.94, -128.59) * mm, "end": v(-78.31, -131.29) * mm});
            skLineSegment(sketch, "E269.MirrorCS", {"start": v(-104.18, 131.98) * mm, "end": v(-97.68, 118.85) * mm});
            skArc(sketch, "E270.MirrorCS", {"start": v(-31.74, -143.57) * mm, "mid": v(-35.31, -144.74) * mm, "end": v(-37.12, -148.05) * mm});
            skLineSegment(sketch, "E271.MirrorCS", {"start": v(-158.47, 60.52) * mm, "end": v(-143.98, 58.2) * mm});
            skArc(sketch, "E272.MirrorCS", {"start": v(-133.7, -78.05) * mm, "mid": v(-130.77, -75.07) * mm, "end": v(-131.07, -70.9) * mm});
            skLineSegment(sketch, "E273.MirrorCS", {"start": v(-163.63, -46.39) * mm, "end": v(-149.95, -39.18) * mm});
            skLineSegment(sketch, "E274.MirrorCS", {"start": v(-166.3, -32.28) * mm, "end": v(-151.62, -32.33) * mm});
            skArc(sketch, "E275.MirrorCS", {"start": v(-123.5, -121.14) * mm, "mid": v(-120.49, -122.95) * mm, "end": v(-117.02, -122.4) * mm});
            skLineSegment(sketch, "E276.MirrorCS", {"start": v(-154.27, -72.54) * mm, "end": v(-142.33, -62.58) * mm});
            skLineSegment(sketch, "E277.MirrorCS", {"start": v(-146.5, -26.47) * mm, "end": v(-147.92, -18.26) * mm});
            skLineSegment(sketch, "E278.MirrorCS", {"start": v(-64.1, -133.27) * mm, "end": v(-70.7, -129.43) * mm});
            skLineSegment(sketch, "E279.MirrorCS", {"start": v(-162.34, 48.75) * mm, "end": v(-149.54, 41.63) * mm});
            skArc(sketch, "E280.MirrorCS", {"start": v(-171.19, -28.11) * mm, "mid": v(-169.48, -31.07) * mm, "end": v(-166.3, -32.28) * mm});
            skArc(sketch, "E281.MirrorCS", {"start": v(-168.9, -20.12) * mm, "mid": v(-171.01, -22.1) * mm, "end": v(-171.71, -24.91) * mm});
            skLineSegment(sketch, "E282.MirrorCS", {"start": v(-86.2, -120.52) * mm, "end": v(-92.12, -115.95) * mm});
            skLineSegment(sketch, "E283.MirrorCS", {"start": v(-131.07, -70.9) * mm, "end": v(-134.76, -64.45) * mm});
            skLineSegment(sketch, "E284.MirrorCS", {"start": v(-97.32, -138.26) * mm, "end": v(-85.9, -127.85) * mm});
            skArc(sketch, "E285.MirrorCS", {"start": v(-154.04, -80.28) * mm, "mid": v(-151.64, -82.85) * mm, "end": v(-148.15, -83.26) * mm});
            skLineSegment(sketch, "E286.MirrorCS", {"start": v(-37.17, -164.2) * mm, "end": v(-37.12, -148.05) * mm});
            skArc(sketch, "E287.MirrorCS", {"start": v(-144.75, -56.07) * mm, "mid": v(-141.14, -53.74) * mm, "end": v(-140.6, -49.48) * mm});
            skLineSegment(sketch, "E288.MirrorCS", {"start": v(-23.39, -145.07) * mm, "end": v(-31.74, -143.57) * mm});
            skLineSegment(sketch, "E289.MirrorCS", {"start": v(-125.73, -113.6) * mm, "end": v(-116.75, -100.86) * mm});
            skLineSegment(sketch, "E290.MirrorCS", {"start": v(-134.74, -103.25) * mm, "end": v(-120.77, -96.8) * mm});
            skLineSegment(sketch, "E291.MirrorCS", {"start": v(-152.5, 74.73) * mm, "end": v(-141.47, 65.1) * mm});
            skArc(sketch, "E292.MirrorCS", {"start": v(-85.9, -127.85) * mm, "mid": v(-84.48, -124.12) * mm, "end": v(-86.2, -120.52) * mm});
            skLineSegment(sketch, "E293.MirrorCS", {"start": v(-168.9, -20.12) * mm, "end": v(-155.12, -15.16) * mm});
            skLineSegment(sketch, "E294.MirrorCS", {"start": v(-24.9, -166.43) * mm, "end": v(-19.52, -151.82) * mm});
            skArc(sketch, "E295.MirrorCS", {"start": v(-125.73, -113.6) * mm, "mid": v(-126.38, -116.53) * mm, "end": v(-125.27, -119.32) * mm});
            skArc(sketch, "E296.MirrorCS", {"start": v(-92.12, -115.95) * mm, "mid": v(-96.22, -114.6) * mm, "end": v(-99.88, -116.87) * mm});
            skLineSegment(sketch, "E297.MirrorCS", {"start": v(-159.28, -58.06) * mm, "end": v(-144.75, -56.07) * mm});
            skArc(sketch, "E298.MirrorCS", {"start": v(-164.82, -54.53) * mm, "mid": v(-162.7, -57.3) * mm, "end": v(-159.28, -58.06) * mm});
            skArc(sketch, "E299.MirrorCS", {"start": v(-27.26, 168.8) * mm, "mid": v(-23.75, 168.55) * mm, "end": v(-21.23, 166.1) * mm});
            skArc(sketch, "E300.MirrorCS", {"start": v(-104.18, 131.98) * mm, "mid": v(-104.34, 134.9) * mm, "end": v(-102.88, 137.42) * mm});
            skLineSegment(sketch, "E301.MirrorCS", {"start": v(-62.7, -157.5) * mm, "end": v(-59.7, -140.76) * mm});
            skArc(sketch, "E302.MirrorCS", {"start": v(-19.52, -151.82) * mm, "mid": v(-19.88, -147.54) * mm, "end": v(-23.39, -145.07) * mm});
            skArc(sketch, "E303.MirrorCS", {"start": v(-154.27, -72.54) * mm, "mid": v(-155.6, -75.15) * mm, "end": v(-155.29, -78.06) * mm});
            skLineSegment(sketch, "E304.MirrorCS", {"start": v(-51.04, -161.8) * mm, "end": v(-42.53, -147.18) * mm});
            skLineSegment(sketch, "E305.MirrorCS", {"start": v(-86.57, -145.06) * mm, "end": v(-78.31, -131.29) * mm});
            skArc(sketch, "E306.MirrorCS", {"start": v(-42.53, -147.18) * mm, "mid": v(-42.55, -142.87) * mm, "end": v(-45.86, -140.11) * mm});
            skLineSegment(sketch, "E307.MirrorCS", {"start": v(-148.15, -83.26) * mm, "end": v(-133.7, -78.05) * mm});
            skLineSegment(sketch, "E308.MirrorCS", {"start": v(-76.06, -151.2) * mm, "end": v(-62.52, -139.03) * mm});
            skLineSegment(sketch, "E309.MirrorCS", {"start": v(-171.19, -28.11) * mm, "end": v(-171.71, -24.91) * mm});
            skArc(sketch, "E310.MirrorCS", {"start": v(-162.34, 48.75) * mm, "mid": v(-164.3, 51.18) * mm, "end": v(-164.47, 54.28) * mm});
            skArc(sketch, "E311.MirrorCS", {"start": v(-108.93, -100.9) * mm, "mid": v(-112.83, -99.05) * mm, "end": v(-116.75, -100.86) * mm});
            skArc(sketch, "E312.MirrorCS", {"start": v(-163.63, -46.39) * mm, "mid": v(-165.45, -48.64) * mm, "end": v(-165.75, -51.53) * mm});
            skArc(sketch, "E313.MirrorCS", {"start": v(-62.52, -139.03) * mm, "mid": v(-62.4, -135.9) * mm, "end": v(-64.1, -133.27) * mm});
            skLineSegment(sketch, "E314.MirrorCS", {"start": v(-103.67, -106.18) * mm, "end": v(-108.93, -100.9) * mm});
            skLineSegment(sketch, "E315.MirrorCS", {"start": v(-140.6, -49.48) * mm, "end": v(-142.87, -42.41) * mm});
            skLineSegment(sketch, "E316.MirrorCS", {"start": v(-117.02, -122.4) * mm, "end": v(-104.35, -113.58) * mm});
            skLineSegment(sketch, "E317.MirrorCS", {"start": v(-154.04, -80.28) * mm, "end": v(-155.29, -78.06) * mm});
            skLineSegment(sketch, "E318.MirrorCS", {"start": v(-107.12, -130.68) * mm, "end": v(-99.88, -116.87) * mm});
            skLineSegment(sketch, "E319.MirrorCS", {"start": v(-123.5, -121.14) * mm, "end": v(-125.27, -119.32) * mm});
            skLineSegment(sketch, "E320.MirrorCS", {"start": v(-45.86, -140.11) * mm, "end": v(-53.6, -137.27) * mm});
            skArc(sketch, "E321.MirrorCS", {"start": v(-142.87, -42.41) * mm, "mid": v(-145.66, -39.14) * mm, "end": v(-149.95, -39.18) * mm});
            skLineSegment(sketch, "E322.MirrorCS", {"start": v(-21.23, 166.1) * mm, "end": v(-16.06, 150.98) * mm});
            skPoint(sketch, "E323.MirrorP", {"position": v(-4.64, 170.28) * mm});
            skLineSegment(sketch, "E324", {"start": v(-377.4, 95.28) * mm, "end": v(-374.86, 95.28) * mm});
            skLineSegment(sketch, "E325", {"start": v(-369.86, 91.13) * mm, "end": v(-367.2, 76.72) * mm});
            skLineSegment(sketch, "E326", {"start": v(-382.4, 91.05) * mm, "end": v(-384.84, 76.58) * mm});
            skLineSegment(sketch, "E327", {"start": v(-379.78, 70.66) * mm, "end": v(-372.15, 70.72) * mm});
            skArc(sketch, "E328.filletArc", {"start": v(-377.4, 95.28) * mm, "mid": v(-380.68, 94.08) * mm, "end": v(-382.4, 91.05) * mm});
            skArc(sketch, "E329.filletArc", {"start": v(-369.86, 91.13) * mm, "mid": v(-371.6, 94.1) * mm, "end": v(-374.86, 95.28) * mm});
            skArc(sketch, "E330.filletArc", {"start": v(-372.15, 70.72) * mm, "mid": v(-368.28, 72.57) * mm, "end": v(-367.2, 76.72) * mm});
            skArc(sketch, "E331.filletArc", {"start": v(-384.84, 76.58) * mm, "mid": v(-383.7, 72.44) * mm, "end": v(-379.78, 70.66) * mm});
            skLineSegment(sketch, "E332", {"start": v(-282.3, 2.5) * mm, "end": v(-282.3, -0.04) * mm});
            skLineSegment(sketch, "E333", {"start": v(-286.45, -5.04) * mm, "end": v(-300.86, -7.7) * mm});
            skLineSegment(sketch, "E334", {"start": v(-286.53, 7.5) * mm, "end": v(-301, 9.94) * mm});
            skLineSegment(sketch, "E335", {"start": v(-306.92, 4.88) * mm, "end": v(-306.86, -2.75) * mm});
            skArc(sketch, "E336.filletArc", {"start": v(-282.3, 2.5) * mm, "mid": v(-283.5, 5.78) * mm, "end": v(-286.53, 7.5) * mm});
            skArc(sketch, "E337.filletArc", {"start": v(-286.45, -5.04) * mm, "mid": v(-283.47, -3.3) * mm, "end": v(-282.3, -0.04) * mm});
            skArc(sketch, "E338.filletArc", {"start": v(-306.86, -2.75) * mm, "mid": v(-305.01, -6.62) * mm, "end": v(-300.86, -7.7) * mm});
            skArc(sketch, "E339.filletArc", {"start": v(-301, 9.94) * mm, "mid": v(-305.14, 8.8) * mm, "end": v(-306.92, 4.88) * mm});
            skLineSegment(sketch, "E340", {"start": v(-347.35, 91.13) * mm, "end": v(-344.96, 90.26) * mm});
            skLineSegment(sketch, "E341", {"start": v(-341.7, 84.65) * mm, "end": v(-344.12, 70.2) * mm});
            skLineSegment(sketch, "E342", {"start": v(-353.5, 88.86) * mm, "end": v(-360.74, 76.1) * mm});
            skLineSegment(sketch, "E343", {"start": v(-358.02, 68.8) * mm, "end": v(-350.82, 66.25) * mm});
            skArc(sketch, "E344.filletArc", {"start": v(-347.35, 91.13) * mm, "mid": v(-350.85, 91.12) * mm, "end": v(-353.5, 88.86) * mm});
            skArc(sketch, "E345.filletArc", {"start": v(-341.7, 84.65) * mm, "mid": v(-342.31, 88.05) * mm, "end": v(-344.96, 90.26) * mm});
            skArc(sketch, "E346.filletArc", {"start": v(-350.82, 66.25) * mm, "mid": v(-346.55, 66.66) * mm, "end": v(-344.12, 70.2) * mm});
            skArc(sketch, "E347.filletArc", {"start": v(-360.74, 76.1) * mm, "mid": v(-361.08, 71.82) * mm, "end": v(-358.02, 68.8) * mm});
            skLineSegment(sketch, "E348", {"start": v(-316.84, 68.51) * mm, "end": v(-324.06, 55.77) * mm});
            skLineSegment(sketch, "E349", {"start": v(-325.34, 75.53) * mm, "end": v(-336.49, 66.02) * mm});
            skLineSegment(sketch, "E350", {"start": v(-336.42, 58.24) * mm, "end": v(-331.72, 54.35) * mm});
            skArc(sketch, "E351.filletArc", {"start": v(-318.77, 75.56) * mm, "mid": v(-322.06, 76.75) * mm, "end": v(-325.34, 75.53) * mm});
            skArc(sketch, "E352.filletArc", {"start": v(-316.84, 68.51) * mm, "mid": v(-316.27, 71.92) * mm, "end": v(-318, 74.9) * mm});
            skArc(sketch, "E353.filletArc", {"start": v(-331.72, 54.35) * mm, "mid": v(-327.56, 53.28) * mm, "end": v(-324.06, 55.77) * mm});
            skArc(sketch, "E354.filletArc", {"start": v(-336.49, 66.02) * mm, "mid": v(-338.27, 62.11) * mm, "end": v(-336.42, 58.24) * mm});
            skLineSegment(sketch, "E355", {"start": v(-299.56, 55.82) * mm, "end": v(-298.2, 53.67) * mm});
            skLineSegment(sketch, "E356", {"start": v(-299.03, 47.23) * mm, "end": v(-309.75, 37.25) * mm});
            skLineSegment(sketch, "E357", {"start": v(-305.83, 57.77) * mm, "end": v(-319.34, 52.06) * mm});
            skLineSegment(sketch, "E358", {"start": v(-321.62, 44.62) * mm, "end": v(-317.48, 38.21) * mm});
            skArc(sketch, "E359.filletArc", {"start": v(-299.56, 55.82) * mm, "mid": v(-302.34, 57.94) * mm, "end": v(-305.83, 57.77) * mm});
            skArc(sketch, "E360.filletArc", {"start": v(-299.03, 47.23) * mm, "mid": v(-297.45, 50.3) * mm, "end": v(-298.2, 53.67) * mm});
            skArc(sketch, "E361.filletArc", {"start": v(-317.48, 38.21) * mm, "mid": v(-313.84, 35.93) * mm, "end": v(-309.75, 37.25) * mm});
            skArc(sketch, "E362.filletArc", {"start": v(-319.34, 52.06) * mm, "mid": v(-322.22, 48.87) * mm, "end": v(-321.62, 44.62) * mm});
            skLineSegment(sketch, "E363", {"start": v(-285.93, 30.11) * mm, "end": v(-285.28, 27.66) * mm});
            skLineSegment(sketch, "E364", {"start": v(-288, 21.76) * mm, "end": v(-301.22, 15.46) * mm});
            skLineSegment(sketch, "E365", {"start": v(-291.33, 33.85) * mm, "end": v(-305.93, 32.45) * mm});
            skLineSegment(sketch, "E366", {"start": v(-310.34, 26.04) * mm, "end": v(-308.3, 18.69) * mm});
            skArc(sketch, "E367.filletArc", {"start": v(-285.93, 30.11) * mm, "mid": v(-287.94, 32.97) * mm, "end": v(-291.33, 33.85) * mm});
            skArc(sketch, "E368.filletArc", {"start": v(-288, 21.76) * mm, "mid": v(-285.57, 24.22) * mm, "end": v(-285.28, 27.66) * mm});
            skArc(sketch, "E369.filletArc", {"start": v(-308.3, 18.69) * mm, "mid": v(-305.52, 15.42) * mm, "end": v(-301.22, 15.46) * mm});
            skArc(sketch, "E370.filletArc", {"start": v(-305.93, 32.45) * mm, "mid": v(-309.63, 30.28) * mm, "end": v(-310.34, 26.04) * mm});
            skArc(sketch, "E371.MirrorCS", {"start": v(-401.02, 66.25) * mm, "mid": v(-405.3, 66.66) * mm, "end": v(-407.73, 70.2) * mm});
            skArc(sketch, "E372.MirrorCS", {"start": v(-434.37, 38.21) * mm, "mid": v(-438, 35.93) * mm, "end": v(-442.09, 37.25) * mm});
            skArc(sketch, "E373.MirrorCS", {"start": v(-410.15, 84.65) * mm, "mid": v(-409.53, 88.05) * mm, "end": v(-406.88, 90.26) * mm});
            skArc(sketch, "E374.MirrorCS", {"start": v(-452.82, 47.23) * mm, "mid": v(-454.4, 50.3) * mm, "end": v(-453.64, 53.67) * mm});
            skArc(sketch, "E375.MirrorCS", {"start": v(-404.5, 91.13) * mm, "mid": v(-401, 91.12) * mm, "end": v(-398.33, 88.86) * mm});
            skArc(sketch, "E376.MirrorCS", {"start": v(-452.28, 55.82) * mm, "mid": v(-449.5, 57.94) * mm, "end": v(-446.02, 57.77) * mm});
            skLineSegment(sketch, "E377.MirrorCS", {"start": v(-430.22, 44.62) * mm, "end": v(-434.37, 38.21) * mm});
            skLineSegment(sketch, "E378.MirrorCS", {"start": v(-393.83, 68.8) * mm, "end": v(-401.02, 66.25) * mm});
            skLineSegment(sketch, "E379.MirrorCS", {"start": v(-452.28, 55.82) * mm, "end": v(-453.64, 53.67) * mm});
            skLineSegment(sketch, "E380.MirrorCS", {"start": v(-404.5, 91.13) * mm, "end": v(-406.88, 90.26) * mm});
            skArc(sketch, "E381.MirrorCS", {"start": v(-415.36, 66.02) * mm, "mid": v(-413.57, 62.11) * mm, "end": v(-415.42, 58.24) * mm});
            skArc(sketch, "E382.MirrorCS", {"start": v(-450.84, 9.94) * mm, "mid": v(-446.7, 8.8) * mm, "end": v(-444.92, 4.88) * mm});
            skLineSegment(sketch, "E383.MirrorCS", {"start": v(-441.5, 26.04) * mm, "end": v(-443.54, 18.69) * mm});
            skLineSegment(sketch, "E384.MirrorCS", {"start": v(-415.42, 58.24) * mm, "end": v(-420.12, 54.35) * mm});
            skLineSegment(sketch, "E385.MirrorCS", {"start": v(-444.92, 4.88) * mm, "end": v(-444.98, -2.75) * mm});
            skArc(sketch, "E386.MirrorCS", {"start": v(-435, 68.51) * mm, "mid": v(-435.58, 71.92) * mm, "end": v(-433.84, 74.9) * mm});
            skArc(sketch, "E387.MirrorCS", {"start": v(-443.54, 18.69) * mm, "mid": v(-446.32, 15.42) * mm, "end": v(-450.62, 15.46) * mm});
            skArc(sketch, "E388.MirrorCS", {"start": v(-420.12, 54.35) * mm, "mid": v(-424.28, 53.28) * mm, "end": v(-427.78, 55.77) * mm});
            skArc(sketch, "E389.MirrorCS", {"start": v(-433.07, 75.56) * mm, "mid": v(-429.78, 76.75) * mm, "end": v(-426.5, 75.53) * mm});
            skArc(sketch, "E390.MirrorCS", {"start": v(-465.9, 30.11) * mm, "mid": v(-463.9, 32.97) * mm, "end": v(-460.52, 33.85) * mm});
            skLineSegment(sketch, "E391.MirrorCS", {"start": v(-433.07, 75.56) * mm, "end": v(-433.84, 74.9) * mm});
            skLineSegment(sketch, "E392.MirrorCS", {"start": v(-465.9, 30.11) * mm, "end": v(-466.56, 27.66) * mm});
            skLineSegment(sketch, "E393.MirrorCS", {"start": v(-469.55, 2.5) * mm, "end": v(-469.55, -0.04) * mm});
            skArc(sketch, "E394.MirrorCS", {"start": v(-391.1, 76.1) * mm, "mid": v(-390.76, 71.82) * mm, "end": v(-393.83, 68.8) * mm});
            skArc(sketch, "E395.MirrorCS", {"start": v(-469.55, 2.5) * mm, "mid": v(-468.34, 5.78) * mm, "end": v(-465.3, 7.5) * mm});
            skArc(sketch, "E396.MirrorCS", {"start": v(-432.5, 52.06) * mm, "mid": v(-429.63, 48.87) * mm, "end": v(-430.22, 44.62) * mm});
            skArc(sketch, "E397.MirrorCS", {"start": v(-463.84, 21.76) * mm, "mid": v(-466.27, 24.22) * mm, "end": v(-466.56, 27.66) * mm});
            skArc(sketch, "E398.MirrorCS", {"start": v(-465.39, -5.04) * mm, "mid": v(-468.37, -3.3) * mm, "end": v(-469.55, -0.04) * mm});
            skLineSegment(sketch, "E399.MirrorCS", {"start": v(-446.02, 57.77) * mm, "end": v(-432.5, 52.06) * mm});
            skLineSegment(sketch, "E400.MirrorCS", {"start": v(-460.52, 33.85) * mm, "end": v(-445.91, 32.45) * mm});
            skLineSegment(sketch, "E401.MirrorCS", {"start": v(-465.3, 7.5) * mm, "end": v(-450.84, 9.94) * mm});
            skArc(sketch, "E402.MirrorCS", {"start": v(-445.91, 32.45) * mm, "mid": v(-442.21, 30.28) * mm, "end": v(-441.5, 26.04) * mm});
            skArc(sketch, "E403.MirrorCS", {"start": v(-444.98, -2.75) * mm, "mid": v(-446.83, -6.62) * mm, "end": v(-450.99, -7.7) * mm});
            skLineSegment(sketch, "E404.MirrorCS", {"start": v(-426.5, 75.53) * mm, "end": v(-415.36, 66.02) * mm});
            skLineSegment(sketch, "E405.MirrorCS", {"start": v(-398.33, 88.86) * mm, "end": v(-391.1, 76.1) * mm});
            skLineSegment(sketch, "E406.MirrorCS", {"start": v(-410.15, 84.65) * mm, "end": v(-407.73, 70.2) * mm});
            skLineSegment(sketch, "E407.MirrorCS", {"start": v(-452.82, 47.23) * mm, "end": v(-442.09, 37.25) * mm});
            skLineSegment(sketch, "E408.MirrorCS", {"start": v(-463.84, 21.76) * mm, "end": v(-450.62, 15.46) * mm});
            skLineSegment(sketch, "E409.MirrorCS", {"start": v(-435, 68.51) * mm, "end": v(-427.78, 55.77) * mm});
            skLineSegment(sketch, "E410.MirrorCS", {"start": v(-465.39, -5.04) * mm, "end": v(-450.99, -7.7) * mm});
            skArc(sketch, "E411.MirrorCS", {"start": v(-319.34, -52.06) * mm, "mid": v(-322.22, -48.87) * mm, "end": v(-321.62, -44.62) * mm});
            skLineSegment(sketch, "E412.MirrorCS", {"start": v(-393.83, -68.8) * mm, "end": v(-401.02, -66.25) * mm});
            skArc(sketch, "E413.MirrorCS", {"start": v(-360.74, -76.1) * mm, "mid": v(-361.08, -71.82) * mm, "end": v(-358.02, -68.8) * mm});
            skArc(sketch, "E414.MirrorCS", {"start": v(-350.82, -66.25) * mm, "mid": v(-346.55, -66.66) * mm, "end": v(-344.12, -70.2) * mm});
            skArc(sketch, "E415.MirrorCS", {"start": v(-317.48, -38.21) * mm, "mid": v(-313.84, -35.93) * mm, "end": v(-309.75, -37.25) * mm});
            skLineSegment(sketch, "E416.MirrorCS", {"start": v(-430.22, -44.62) * mm, "end": v(-434.37, -38.21) * mm});
            skLineSegment(sketch, "E417.MirrorCS", {"start": v(-465.9, -30.11) * mm, "end": v(-466.56, -27.66) * mm});
            skArc(sketch, "E418.MirrorCS", {"start": v(-432.5, -52.06) * mm, "mid": v(-429.63, -48.87) * mm, "end": v(-430.22, -44.62) * mm});
            skLineSegment(sketch, "E419.MirrorCS", {"start": v(-404.5, -91.13) * mm, "end": v(-406.88, -90.26) * mm});
            skArc(sketch, "E420.MirrorCS", {"start": v(-341.7, -84.65) * mm, "mid": v(-342.31, -88.05) * mm, "end": v(-344.96, -90.26) * mm});
            skArc(sketch, "E421.MirrorCS", {"start": v(-299.03, -47.23) * mm, "mid": v(-297.45, -50.3) * mm, "end": v(-298.2, -53.67) * mm});
            skArc(sketch, "E422.MirrorCS", {"start": v(-452.28, -55.82) * mm, "mid": v(-449.5, -57.94) * mm, "end": v(-446.02, -57.77) * mm});
            skLineSegment(sketch, "E423.MirrorCS", {"start": v(-433.07, -75.56) * mm, "end": v(-433.84, -74.9) * mm});
            skArc(sketch, "E424.MirrorCS", {"start": v(-347.35, -91.13) * mm, "mid": v(-350.85, -91.12) * mm, "end": v(-353.5, -88.86) * mm});
            skArc(sketch, "E425.MirrorCS", {"start": v(-404.5, -91.13) * mm, "mid": v(-401, -91.12) * mm, "end": v(-398.33, -88.86) * mm});
            skArc(sketch, "E426.MirrorCS", {"start": v(-299.56, -55.82) * mm, "mid": v(-302.34, -57.94) * mm, "end": v(-305.83, -57.77) * mm});
            skArc(sketch, "E427.MirrorCS", {"start": v(-465.9, -30.11) * mm, "mid": v(-463.9, -32.97) * mm, "end": v(-460.52, -33.85) * mm});
            skArc(sketch, "E428.MirrorCS", {"start": v(-369.86, -91.13) * mm, "mid": v(-371.6, -94.1) * mm, "end": v(-374.86, -95.28) * mm});
            skLineSegment(sketch, "E429.MirrorCS", {"start": v(-358.02, -68.8) * mm, "end": v(-350.82, -66.25) * mm});
            skLineSegment(sketch, "E430.MirrorCS", {"start": v(-321.62, -44.62) * mm, "end": v(-317.48, -38.21) * mm});
            skArc(sketch, "E431.MirrorCS", {"start": v(-452.82, -47.23) * mm, "mid": v(-454.4, -50.3) * mm, "end": v(-453.64, -53.67) * mm});
            skArc(sketch, "E432.MirrorCS", {"start": v(-433.07, -75.56) * mm, "mid": v(-429.78, -76.75) * mm, "end": v(-426.5, -75.53) * mm});
            skArc(sketch, "E433.MirrorCS", {"start": v(-377.4, -95.28) * mm, "mid": v(-380.68, -94.08) * mm, "end": v(-382.4, -91.05) * mm});
            skArc(sketch, "E434.MirrorCS", {"start": v(-410.15, -84.65) * mm, "mid": v(-409.53, -88.05) * mm, "end": v(-406.88, -90.26) * mm});
            skArc(sketch, "E435.MirrorCS", {"start": v(-420.12, -54.35) * mm, "mid": v(-424.28, -53.28) * mm, "end": v(-427.78, -55.77) * mm});
            skLineSegment(sketch, "E436.MirrorCS", {"start": v(-379.78, -70.66) * mm, "end": v(-372.15, -70.72) * mm});
            skArc(sketch, "E437.MirrorCS", {"start": v(-434.37, -38.21) * mm, "mid": v(-438, -35.93) * mm, "end": v(-442.09, -37.25) * mm});
            skLineSegment(sketch, "E438.MirrorCS", {"start": v(-299.56, -55.82) * mm, "end": v(-298.2, -53.67) * mm});
            skArc(sketch, "E439.MirrorCS", {"start": v(-401.02, -66.25) * mm, "mid": v(-405.3, -66.66) * mm, "end": v(-407.73, -70.2) * mm});
            skLineSegment(sketch, "E440.MirrorCS", {"start": v(-347.35, -91.13) * mm, "end": v(-344.96, -90.26) * mm});
            skArc(sketch, "E441.MirrorCS", {"start": v(-435, -68.51) * mm, "mid": v(-435.58, -71.92) * mm, "end": v(-433.84, -74.9) * mm});
            skArc(sketch, "E442.MirrorCS", {"start": v(-445.91, -32.45) * mm, "mid": v(-442.21, -30.28) * mm, "end": v(-441.5, -26.04) * mm});
            skLineSegment(sketch, "E443.MirrorCS", {"start": v(-441.5, -26.04) * mm, "end": v(-443.54, -18.69) * mm});
            skArc(sketch, "E444.MirrorCS", {"start": v(-336.49, -66.02) * mm, "mid": v(-338.27, -62.11) * mm, "end": v(-336.42, -58.24) * mm});
            skArc(sketch, "E445.MirrorCS", {"start": v(-318.77, -75.56) * mm, "mid": v(-322.06, -76.75) * mm, "end": v(-325.34, -75.53) * mm});
            skArc(sketch, "E446.MirrorCS", {"start": v(-285.93, -30.11) * mm, "mid": v(-287.94, -32.97) * mm, "end": v(-291.33, -33.85) * mm});
            skLineSegment(sketch, "E447.MirrorCS", {"start": v(-310.34, -26.04) * mm, "end": v(-308.3, -18.69) * mm});
            skLineSegment(sketch, "E448.MirrorCS", {"start": v(-336.42, -58.24) * mm, "end": v(-331.72, -54.35) * mm});
            skArc(sketch, "E449.MirrorCS", {"start": v(-331.72, -54.35) * mm, "mid": v(-327.56, -53.28) * mm, "end": v(-324.06, -55.77) * mm});
            skArc(sketch, "E450.MirrorCS", {"start": v(-463.84, -21.76) * mm, "mid": v(-466.27, -24.22) * mm, "end": v(-466.56, -27.66) * mm});
            skArc(sketch, "E451.MirrorCS", {"start": v(-415.36, -66.02) * mm, "mid": v(-413.57, -62.11) * mm, "end": v(-415.42, -58.24) * mm});
            skArc(sketch, "E452.MirrorCS", {"start": v(-316.84, -68.51) * mm, "mid": v(-316.27, -71.92) * mm, "end": v(-318, -74.9) * mm});
            skLineSegment(sketch, "E453.MirrorCS", {"start": v(-415.42, -58.24) * mm, "end": v(-420.12, -54.35) * mm});
            skArc(sketch, "E454.MirrorCS", {"start": v(-288, -21.76) * mm, "mid": v(-285.57, -24.22) * mm, "end": v(-285.28, -27.66) * mm});
            skLineSegment(sketch, "E455.MirrorCS", {"start": v(-318.77, -75.56) * mm, "end": v(-318, -74.9) * mm});
            skLineSegment(sketch, "E456.MirrorCS", {"start": v(-452.28, -55.82) * mm, "end": v(-453.64, -53.67) * mm});
            skLineSegment(sketch, "E457.MirrorCS", {"start": v(-285.93, -30.11) * mm, "end": v(-285.28, -27.66) * mm});
            skLineSegment(sketch, "E458.MirrorCS", {"start": v(-377.4, -95.28) * mm, "end": v(-374.86, -95.28) * mm});
            skArc(sketch, "E459.MirrorCS", {"start": v(-391.1, -76.1) * mm, "mid": v(-390.76, -71.82) * mm, "end": v(-393.83, -68.8) * mm});
            skArc(sketch, "E460.MirrorCS", {"start": v(-384.84, -76.58) * mm, "mid": v(-383.7, -72.44) * mm, "end": v(-379.78, -70.66) * mm});
            skArc(sketch, "E461.MirrorCS", {"start": v(-372.15, -70.72) * mm, "mid": v(-368.28, -72.57) * mm, "end": v(-367.2, -76.72) * mm});
            skLineSegment(sketch, "E462.MirrorCS", {"start": v(-305.83, -57.77) * mm, "end": v(-319.34, -52.06) * mm});
            skArc(sketch, "E463.MirrorCS", {"start": v(-305.93, -32.45) * mm, "mid": v(-309.63, -30.28) * mm, "end": v(-310.34, -26.04) * mm});
            skLineSegment(sketch, "E464.MirrorCS", {"start": v(-291.33, -33.85) * mm, "end": v(-305.93, -32.45) * mm});
            skLineSegment(sketch, "E465.MirrorCS", {"start": v(-435, -68.51) * mm, "end": v(-427.78, -55.77) * mm});
            skLineSegment(sketch, "E466.MirrorCS", {"start": v(-316.84, -68.51) * mm, "end": v(-324.06, -55.77) * mm});
            skLineSegment(sketch, "E467.MirrorCS", {"start": v(-288, -21.76) * mm, "end": v(-301.22, -15.46) * mm});
            skLineSegment(sketch, "E468.MirrorCS", {"start": v(-463.84, -21.76) * mm, "end": v(-450.62, -15.46) * mm});
            skLineSegment(sketch, "E469.MirrorCS", {"start": v(-452.82, -47.23) * mm, "end": v(-442.09, -37.25) * mm});
            skLineSegment(sketch, "E470.MirrorCS", {"start": v(-410.15, -84.65) * mm, "end": v(-407.73, -70.2) * mm});
            skLineSegment(sketch, "E471.MirrorCS", {"start": v(-353.5, -88.86) * mm, "end": v(-360.74, -76.1) * mm});
            skLineSegment(sketch, "E472.MirrorCS", {"start": v(-398.33, -88.86) * mm, "end": v(-391.1, -76.1) * mm});
            skLineSegment(sketch, "E473.MirrorCS", {"start": v(-426.5, -75.53) * mm, "end": v(-415.36, -66.02) * mm});
            skLineSegment(sketch, "E474.MirrorCS", {"start": v(-341.7, -84.65) * mm, "end": v(-344.12, -70.2) * mm});
            skLineSegment(sketch, "E475.MirrorCS", {"start": v(-299.03, -47.23) * mm, "end": v(-309.75, -37.25) * mm});
            skLineSegment(sketch, "E476.MirrorCS", {"start": v(-382.4, -91.05) * mm, "end": v(-384.84, -76.58) * mm});
            skLineSegment(sketch, "E477.MirrorCS", {"start": v(-446.02, -57.77) * mm, "end": v(-432.5, -52.06) * mm});
            skLineSegment(sketch, "E478.MirrorCS", {"start": v(-369.86, -91.13) * mm, "end": v(-367.2, -76.72) * mm});
            skLineSegment(sketch, "E479.MirrorCS", {"start": v(-460.52, -33.85) * mm, "end": v(-445.91, -32.45) * mm});
            skLineSegment(sketch, "E480.MirrorCS", {"start": v(-325.34, -75.53) * mm, "end": v(-336.49, -66.02) * mm});
            skArc(sketch, "E481.MirrorCS", {"start": v(-443.54, -18.69) * mm, "mid": v(-446.32, -15.42) * mm, "end": v(-450.62, -15.46) * mm});
            skArc(sketch, "E482.MirrorCS", {"start": v(-308.3, -18.69) * mm, "mid": v(-305.52, -15.42) * mm, "end": v(-301.22, -15.46) * mm});
            skCircle(sketch, "E483", {"center": v(257.55, -43.32) * mm, "radius": 76.2 * mm});
            skCircle(sketch, "E484", {"center": v(257.55, -43.32) * mm, "radius": 6.35 * mm});
            skLineSegment(sketch, "E485", {"start": v(256.08, 51.97) * mm, "end": v(258.62, 51.97) * mm});
            skLineSegment(sketch, "E486", {"start": v(263.61, 47.81) * mm, "end": v(266.27, 33.4) * mm});
            skLineSegment(sketch, "E487", {"start": v(251.07, 47.73) * mm, "end": v(248.64, 33.26) * mm});
            skLineSegment(sketch, "E488", {"start": v(253.7, 27.34) * mm, "end": v(261.32, 27.4) * mm});
            skArc(sketch, "E489.filletArc", {"start": v(256.08, 51.97) * mm, "mid": v(252.8, 50.77) * mm, "end": v(251.07, 47.73) * mm});
            skArc(sketch, "E490.filletArc", {"start": v(263.61, 47.81) * mm, "mid": v(261.87, 50.8) * mm, "end": v(258.62, 51.97) * mm});
            skArc(sketch, "E491.filletArc", {"start": v(261.32, 27.4) * mm, "mid": v(265.2, 29.25) * mm, "end": v(266.27, 33.4) * mm});
            skArc(sketch, "E492.filletArc", {"start": v(248.64, 33.26) * mm, "mid": v(249.78, 29.12) * mm, "end": v(253.7, 27.34) * mm});
            skLineSegment(sketch, "E493", {"start": v(351.18, -40.82) * mm, "end": v(351.18, -43.36) * mm});
            skLineSegment(sketch, "E494", {"start": v(347.02, -48.35) * mm, "end": v(332.62, -51.02) * mm});
            skLineSegment(sketch, "E495", {"start": v(346.94, -35.8) * mm, "end": v(332.47, -33.38) * mm});
            skLineSegment(sketch, "E496", {"start": v(326.55, -38.43) * mm, "end": v(326.62, -46.06) * mm});
            skArc(sketch, "E497.filletArc", {"start": v(351.18, -40.82) * mm, "mid": v(349.98, -37.54) * mm, "end": v(346.94, -35.8) * mm});
            skArc(sketch, "E498.filletArc", {"start": v(347.02, -48.35) * mm, "mid": v(350, -46.6) * mm, "end": v(351.18, -43.36) * mm});
            skArc(sketch, "E499.filletArc", {"start": v(326.62, -46.06) * mm, "mid": v(328.46, -49.94) * mm, "end": v(332.62, -51.02) * mm});
            skArc(sketch, "E500.filletArc", {"start": v(332.47, -33.38) * mm, "mid": v(328.33, -34.53) * mm, "end": v(326.55, -38.43) * mm});
            skLineSegment(sketch, "E501", {"start": v(286.12, 47.81) * mm, "end": v(288.51, 46.94) * mm});
            skLineSegment(sketch, "E502", {"start": v(291.78, 41.33) * mm, "end": v(289.36, 26.88) * mm});
            skLineSegment(sketch, "E503", {"start": v(279.97, 45.54) * mm, "end": v(272.74, 32.78) * mm});
            skLineSegment(sketch, "E504", {"start": v(275.46, 25.49) * mm, "end": v(282.65, 22.94) * mm});
            skArc(sketch, "E505.filletArc", {"start": v(286.12, 47.81) * mm, "mid": v(282.63, 47.8) * mm, "end": v(279.97, 45.54) * mm});
            skArc(sketch, "E506.filletArc", {"start": v(291.78, 41.33) * mm, "mid": v(291.16, 44.73) * mm, "end": v(288.51, 46.94) * mm});
            skArc(sketch, "E507.filletArc", {"start": v(282.65, 22.94) * mm, "mid": v(286.92, 23.35) * mm, "end": v(289.36, 26.88) * mm});
            skArc(sketch, "E508.filletArc", {"start": v(272.74, 32.78) * mm, "mid": v(272.4, 28.5) * mm, "end": v(275.46, 25.49) * mm});
            skLineSegment(sketch, "E509", {"start": v(314.7, 32.24) * mm, "end": v(315.48, 31.6) * mm});
            skLineSegment(sketch, "E510", {"start": v(316.63, 25.2) * mm, "end": v(309.41, 12.45) * mm});
            skLineSegment(sketch, "E511", {"start": v(308.14, 32.21) * mm, "end": v(296.99, 22.7) * mm});
            skLineSegment(sketch, "E512", {"start": v(297.05, 14.92) * mm, "end": v(301.76, 11.04) * mm});
            skArc(sketch, "E513.filletArc", {"start": v(314.7, 32.24) * mm, "mid": v(311.41, 33.43) * mm, "end": v(308.14, 32.21) * mm});
            skArc(sketch, "E514.filletArc", {"start": v(316.63, 25.2) * mm, "mid": v(317.2, 28.6) * mm, "end": v(315.48, 31.6) * mm});
            skArc(sketch, "E515.filletArc", {"start": v(301.76, 11.04) * mm, "mid": v(305.91, 9.96) * mm, "end": v(309.41, 12.45) * mm});
            skArc(sketch, "E516.filletArc", {"start": v(296.99, 22.7) * mm, "mid": v(295.2, 18.8) * mm, "end": v(297.05, 14.92) * mm});
            skLineSegment(sketch, "E517", {"start": v(333.91, 12.5) * mm, "end": v(335.28, 10.36) * mm});
            skLineSegment(sketch, "E518", {"start": v(334.45, 3.91) * mm, "end": v(323.72, -6.06) * mm});
            skLineSegment(sketch, "E519", {"start": v(327.65, 14.45) * mm, "end": v(314.14, 8.74) * mm});
            skLineSegment(sketch, "E520", {"start": v(311.85, 1.3) * mm, "end": v(316, -5.1) * mm});
            skArc(sketch, "E521.filletArc", {"start": v(333.91, 12.5) * mm, "mid": v(331.14, 14.62) * mm, "end": v(327.65, 14.45) * mm});
            skArc(sketch, "E522.filletArc", {"start": v(334.45, 3.91) * mm, "mid": v(336.03, 6.98) * mm, "end": v(335.28, 10.36) * mm});
            skArc(sketch, "E523.filletArc", {"start": v(316, -5.1) * mm, "mid": v(319.64, -7.39) * mm, "end": v(323.72, -6.06) * mm});
            skArc(sketch, "E524.filletArc", {"start": v(314.14, 8.74) * mm, "mid": v(311.26, 5.55) * mm, "end": v(311.85, 1.3) * mm});
            skLineSegment(sketch, "E525", {"start": v(347.54, -13.2) * mm, "end": v(348.2, -15.66) * mm});
            skLineSegment(sketch, "E526", {"start": v(345.48, -21.56) * mm, "end": v(332.25, -27.86) * mm});
            skLineSegment(sketch, "E527", {"start": v(342.15, -9.46) * mm, "end": v(327.55, -10.86) * mm});
            skLineSegment(sketch, "E528", {"start": v(323.13, -17.27) * mm, "end": v(325.17, -24.63) * mm});
            skArc(sketch, "E529.filletArc", {"start": v(347.54, -13.2) * mm, "mid": v(345.53, -10.35) * mm, "end": v(342.15, -9.46) * mm});
            skArc(sketch, "E530.filletArc", {"start": v(345.48, -21.56) * mm, "mid": v(347.9, -19.1) * mm, "end": v(348.2, -15.66) * mm});
            skArc(sketch, "E531.filletArc", {"start": v(325.17, -24.63) * mm, "mid": v(327.96, -27.9) * mm, "end": v(332.25, -27.86) * mm});
            skArc(sketch, "E532.filletArc", {"start": v(327.55, -10.86) * mm, "mid": v(323.85, -13.04) * mm, "end": v(323.13, -17.27) * mm});
            skArc(sketch, "E533.MirrorCS", {"start": v(232.46, 22.94) * mm, "mid": v(228.18, 23.35) * mm, "end": v(225.75, 26.88) * mm});
            skArc(sketch, "E534.MirrorCS", {"start": v(199.1, -5.1) * mm, "mid": v(195.47, -7.39) * mm, "end": v(191.39, -6.06) * mm});
            skArc(sketch, "E535.MirrorCS", {"start": v(223.32, 41.33) * mm, "mid": v(223.95, 44.73) * mm, "end": v(226.6, 46.94) * mm});
            skArc(sketch, "E536.MirrorCS", {"start": v(180.66, 3.91) * mm, "mid": v(179.08, 6.98) * mm, "end": v(179.83, 10.36) * mm});
            skArc(sketch, "E537.MirrorCS", {"start": v(228.98, 47.81) * mm, "mid": v(232.48, 47.8) * mm, "end": v(235.14, 45.54) * mm});
            skArc(sketch, "E538.MirrorCS", {"start": v(181.2, 12.5) * mm, "mid": v(183.97, 14.62) * mm, "end": v(187.46, 14.45) * mm});
            skLineSegment(sketch, "E539.MirrorCS", {"start": v(203.26, 1.3) * mm, "end": v(199.1, -5.1) * mm});
            skLineSegment(sketch, "E540.MirrorCS", {"start": v(239.65, 25.49) * mm, "end": v(232.46, 22.94) * mm});
            skLineSegment(sketch, "E541.MirrorCS", {"start": v(181.2, 12.5) * mm, "end": v(179.83, 10.36) * mm});
            skLineSegment(sketch, "E542.MirrorCS", {"start": v(228.98, 47.81) * mm, "end": v(226.6, 46.94) * mm});
            skArc(sketch, "E543.MirrorCS", {"start": v(218.12, 22.7) * mm, "mid": v(219.9, 18.8) * mm, "end": v(218.05, 14.92) * mm});
            skArc(sketch, "E544.MirrorCS", {"start": v(182.63, -33.38) * mm, "mid": v(186.77, -34.53) * mm, "end": v(188.56, -38.43) * mm});
            skLineSegment(sketch, "E545.MirrorCS", {"start": v(191.97, -17.27) * mm, "end": v(189.94, -24.63) * mm});
            skLineSegment(sketch, "E546.MirrorCS", {"start": v(218.05, 14.92) * mm, "end": v(213.35, 11.04) * mm});
            skLineSegment(sketch, "E547.MirrorCS", {"start": v(188.56, -38.43) * mm, "end": v(188.5, -46.06) * mm});
            skArc(sketch, "E548.MirrorCS", {"start": v(198.48, 25.2) * mm, "mid": v(197.9, 28.6) * mm, "end": v(199.63, 31.6) * mm});
            skArc(sketch, "E549.MirrorCS", {"start": v(189.94, -24.63) * mm, "mid": v(187.15, -27.9) * mm, "end": v(182.86, -27.86) * mm});
            skArc(sketch, "E550.MirrorCS", {"start": v(213.35, 11.04) * mm, "mid": v(209.2, 9.96) * mm, "end": v(205.7, 12.45) * mm});
            skArc(sketch, "E551.MirrorCS", {"start": v(200.4, 32.24) * mm, "mid": v(203.7, 33.43) * mm, "end": v(206.97, 32.21) * mm});
            skArc(sketch, "E552.MirrorCS", {"start": v(167.57, -13.2) * mm, "mid": v(169.58, -10.35) * mm, "end": v(172.96, -9.46) * mm});
            skLineSegment(sketch, "E553.MirrorCS", {"start": v(200.4, 32.24) * mm, "end": v(199.63, 31.6) * mm});
            skLineSegment(sketch, "E554.MirrorCS", {"start": v(167.57, -13.2) * mm, "end": v(166.91, -15.66) * mm});
            skLineSegment(sketch, "E555.MirrorCS", {"start": v(163.93, -40.82) * mm, "end": v(163.93, -43.36) * mm});
            skArc(sketch, "E556.MirrorCS", {"start": v(242.37, 32.78) * mm, "mid": v(242.71, 28.5) * mm, "end": v(239.65, 25.49) * mm});
            skArc(sketch, "E557.MirrorCS", {"start": v(163.93, -40.82) * mm, "mid": v(165.13, -37.54) * mm, "end": v(168.17, -35.8) * mm});
            skArc(sketch, "E558.MirrorCS", {"start": v(200.97, 8.74) * mm, "mid": v(203.85, 5.55) * mm, "end": v(203.26, 1.3) * mm});
            skArc(sketch, "E559.MirrorCS", {"start": v(169.63, -21.56) * mm, "mid": v(167.2, -19.1) * mm, "end": v(166.91, -15.66) * mm});
            skArc(sketch, "E560.MirrorCS", {"start": v(168.09, -48.35) * mm, "mid": v(165.1, -46.6) * mm, "end": v(163.93, -43.36) * mm});
            skLineSegment(sketch, "E561.MirrorCS", {"start": v(187.46, 14.45) * mm, "end": v(200.97, 8.74) * mm});
            skLineSegment(sketch, "E562.MirrorCS", {"start": v(172.96, -9.46) * mm, "end": v(187.56, -10.86) * mm});
            skLineSegment(sketch, "E563.MirrorCS", {"start": v(168.17, -35.8) * mm, "end": v(182.63, -33.38) * mm});
            skArc(sketch, "E564.MirrorCS", {"start": v(187.56, -10.86) * mm, "mid": v(191.26, -13.04) * mm, "end": v(191.97, -17.27) * mm});
            skArc(sketch, "E565.MirrorCS", {"start": v(188.5, -46.06) * mm, "mid": v(186.65, -49.94) * mm, "end": v(182.49, -51.02) * mm});
            skLineSegment(sketch, "E566.MirrorCS", {"start": v(206.97, 32.21) * mm, "end": v(218.12, 22.7) * mm});
            skLineSegment(sketch, "E567.MirrorCS", {"start": v(235.14, 45.54) * mm, "end": v(242.37, 32.78) * mm});
            skLineSegment(sketch, "E568.MirrorCS", {"start": v(223.32, 41.33) * mm, "end": v(225.75, 26.88) * mm});
            skLineSegment(sketch, "E569.MirrorCS", {"start": v(180.66, 3.91) * mm, "end": v(191.39, -6.06) * mm});
            skLineSegment(sketch, "E570.MirrorCS", {"start": v(169.63, -21.56) * mm, "end": v(182.86, -27.86) * mm});
            skLineSegment(sketch, "E571.MirrorCS", {"start": v(198.48, 25.2) * mm, "end": v(205.7, 12.45) * mm});
            skLineSegment(sketch, "E572.MirrorCS", {"start": v(168.09, -48.35) * mm, "end": v(182.49, -51.02) * mm});
            skArc(sketch, "E573.MirrorCS", {"start": v(314.14, -95.37) * mm, "mid": v(311.26, -92.19) * mm, "end": v(311.85, -87.93) * mm});
            skLineSegment(sketch, "E574.MirrorCS", {"start": v(239.65, -112.12) * mm, "end": v(232.46, -109.57) * mm});
            skArc(sketch, "E575.MirrorCS", {"start": v(272.74, -119.41) * mm, "mid": v(272.4, -115.13) * mm, "end": v(275.46, -112.12) * mm});
            skArc(sketch, "E576.MirrorCS", {"start": v(282.65, -109.57) * mm, "mid": v(286.92, -109.98) * mm, "end": v(289.36, -113.52) * mm});
            skArc(sketch, "E577.MirrorCS", {"start": v(316, -81.53) * mm, "mid": v(319.64, -79.25) * mm, "end": v(323.72, -80.57) * mm});
            skLineSegment(sketch, "E578.MirrorCS", {"start": v(203.26, -87.93) * mm, "end": v(199.1, -81.53) * mm});
            skLineSegment(sketch, "E579.MirrorCS", {"start": v(167.57, -73.43) * mm, "end": v(166.91, -70.97) * mm});
            skArc(sketch, "E580.MirrorCS", {"start": v(200.97, -95.37) * mm, "mid": v(203.85, -92.19) * mm, "end": v(203.26, -87.93) * mm});
            skLineSegment(sketch, "E581.MirrorCS", {"start": v(228.98, -134.45) * mm, "end": v(226.6, -133.58) * mm});
            skArc(sketch, "E582.MirrorCS", {"start": v(291.78, -127.96) * mm, "mid": v(291.16, -131.36) * mm, "end": v(288.51, -133.58) * mm});
            skArc(sketch, "E583.MirrorCS", {"start": v(334.45, -90.55) * mm, "mid": v(336.03, -93.62) * mm, "end": v(335.28, -97) * mm});
            skArc(sketch, "E584.MirrorCS", {"start": v(181.2, -99.13) * mm, "mid": v(183.97, -101.26) * mm, "end": v(187.46, -101.09) * mm});
            skLineSegment(sketch, "E585.MirrorCS", {"start": v(200.4, -118.88) * mm, "end": v(199.63, -118.23) * mm});
            skArc(sketch, "E586.MirrorCS", {"start": v(286.12, -134.45) * mm, "mid": v(282.63, -134.44) * mm, "end": v(279.97, -132.18) * mm});
            skArc(sketch, "E587.MirrorCS", {"start": v(228.98, -134.45) * mm, "mid": v(232.48, -134.44) * mm, "end": v(235.14, -132.18) * mm});
            skArc(sketch, "E588.MirrorCS", {"start": v(333.91, -99.13) * mm, "mid": v(331.14, -101.26) * mm, "end": v(327.65, -101.09) * mm});
            skArc(sketch, "E589.MirrorCS", {"start": v(167.57, -73.43) * mm, "mid": v(169.58, -76.29) * mm, "end": v(172.96, -77.17) * mm});
            skArc(sketch, "E590.MirrorCS", {"start": v(263.61, -134.44) * mm, "mid": v(261.87, -137.43) * mm, "end": v(258.62, -138.6) * mm});
            skLineSegment(sketch, "E591.MirrorCS", {"start": v(275.46, -112.12) * mm, "end": v(282.65, -109.57) * mm});
            skLineSegment(sketch, "E592.MirrorCS", {"start": v(311.85, -87.93) * mm, "end": v(316, -81.53) * mm});
            skArc(sketch, "E593.MirrorCS", {"start": v(180.66, -90.55) * mm, "mid": v(179.08, -93.62) * mm, "end": v(179.83, -97) * mm});
            skArc(sketch, "E594.MirrorCS", {"start": v(200.4, -118.88) * mm, "mid": v(203.7, -120.06) * mm, "end": v(206.97, -118.85) * mm});
            skArc(sketch, "E595.MirrorCS", {"start": v(256.08, -138.6) * mm, "mid": v(252.8, -137.4) * mm, "end": v(251.07, -134.36) * mm});
            skArc(sketch, "E596.MirrorCS", {"start": v(223.32, -127.96) * mm, "mid": v(223.95, -131.36) * mm, "end": v(226.6, -133.58) * mm});
            skArc(sketch, "E597.MirrorCS", {"start": v(213.35, -97.67) * mm, "mid": v(209.2, -96.6) * mm, "end": v(205.7, -99.09) * mm});
            skLineSegment(sketch, "E598.MirrorCS", {"start": v(253.7, -113.97) * mm, "end": v(261.32, -114.04) * mm});
            skArc(sketch, "E599.MirrorCS", {"start": v(199.1, -81.53) * mm, "mid": v(195.47, -79.25) * mm, "end": v(191.39, -80.57) * mm});
            skLineSegment(sketch, "E600.MirrorCS", {"start": v(333.91, -99.13) * mm, "end": v(335.28, -97) * mm});
            skArc(sketch, "E601.MirrorCS", {"start": v(232.46, -109.57) * mm, "mid": v(228.18, -109.98) * mm, "end": v(225.75, -113.52) * mm});
            skLineSegment(sketch, "E602.MirrorCS", {"start": v(286.12, -134.45) * mm, "end": v(288.51, -133.58) * mm});
            skArc(sketch, "E603.MirrorCS", {"start": v(198.48, -111.83) * mm, "mid": v(197.9, -115.24) * mm, "end": v(199.63, -118.23) * mm});
            skArc(sketch, "E604.MirrorCS", {"start": v(187.56, -75.77) * mm, "mid": v(191.26, -73.6) * mm, "end": v(191.97, -69.36) * mm});
            skLineSegment(sketch, "E605.MirrorCS", {"start": v(191.97, -69.36) * mm, "end": v(189.94, -62) * mm});
            skArc(sketch, "E606.MirrorCS", {"start": v(296.99, -109.34) * mm, "mid": v(295.2, -105.43) * mm, "end": v(297.05, -101.55) * mm});
            skArc(sketch, "E607.MirrorCS", {"start": v(314.7, -118.88) * mm, "mid": v(311.41, -120.06) * mm, "end": v(308.14, -118.85) * mm});
            skArc(sketch, "E608.MirrorCS", {"start": v(347.54, -73.43) * mm, "mid": v(345.53, -76.29) * mm, "end": v(342.15, -77.17) * mm});
            skLineSegment(sketch, "E609.MirrorCS", {"start": v(323.13, -69.36) * mm, "end": v(325.17, -62) * mm});
            skLineSegment(sketch, "E610.MirrorCS", {"start": v(297.05, -101.55) * mm, "end": v(301.76, -97.67) * mm});
            skArc(sketch, "E611.MirrorCS", {"start": v(301.76, -97.67) * mm, "mid": v(305.91, -96.6) * mm, "end": v(309.41, -99.09) * mm});
            skArc(sketch, "E612.MirrorCS", {"start": v(169.63, -65.07) * mm, "mid": v(167.2, -67.53) * mm, "end": v(166.91, -70.97) * mm});
            skArc(sketch, "E613.MirrorCS", {"start": v(218.12, -109.34) * mm, "mid": v(219.9, -105.43) * mm, "end": v(218.05, -101.55) * mm});
            skArc(sketch, "E614.MirrorCS", {"start": v(316.63, -111.83) * mm, "mid": v(317.2, -115.24) * mm, "end": v(315.48, -118.23) * mm});
            skLineSegment(sketch, "E615.MirrorCS", {"start": v(218.05, -101.55) * mm, "end": v(213.35, -97.67) * mm});
            skArc(sketch, "E616.MirrorCS", {"start": v(345.48, -65.07) * mm, "mid": v(347.9, -67.53) * mm, "end": v(348.2, -70.97) * mm});
            skLineSegment(sketch, "E617.MirrorCS", {"start": v(314.7, -118.88) * mm, "end": v(315.48, -118.23) * mm});
            skLineSegment(sketch, "E618.MirrorCS", {"start": v(181.2, -99.13) * mm, "end": v(179.83, -97) * mm});
            skLineSegment(sketch, "E619.MirrorCS", {"start": v(347.54, -73.43) * mm, "end": v(348.2, -70.97) * mm});
            skLineSegment(sketch, "E620.MirrorCS", {"start": v(256.08, -138.6) * mm, "end": v(258.62, -138.6) * mm});
            skArc(sketch, "E621.MirrorCS", {"start": v(242.37, -119.41) * mm, "mid": v(242.71, -115.13) * mm, "end": v(239.65, -112.12) * mm});
            skArc(sketch, "E622.MirrorCS", {"start": v(248.64, -119.9) * mm, "mid": v(249.78, -115.76) * mm, "end": v(253.7, -113.97) * mm});
            skArc(sketch, "E623.MirrorCS", {"start": v(261.32, -114.04) * mm, "mid": v(265.2, -115.88) * mm, "end": v(266.27, -120.04) * mm});
            skLineSegment(sketch, "E624.MirrorCS", {"start": v(327.65, -101.09) * mm, "end": v(314.14, -95.37) * mm});
            skArc(sketch, "E625.MirrorCS", {"start": v(327.55, -75.77) * mm, "mid": v(323.85, -73.6) * mm, "end": v(323.13, -69.36) * mm});
            skLineSegment(sketch, "E626.MirrorCS", {"start": v(342.15, -77.17) * mm, "end": v(327.55, -75.77) * mm});
            skLineSegment(sketch, "E627.MirrorCS", {"start": v(198.48, -111.83) * mm, "end": v(205.7, -99.09) * mm});
            skLineSegment(sketch, "E628.MirrorCS", {"start": v(316.63, -111.83) * mm, "end": v(309.41, -99.09) * mm});
            skLineSegment(sketch, "E629.MirrorCS", {"start": v(345.48, -65.07) * mm, "end": v(332.25, -58.77) * mm});
            skLineSegment(sketch, "E630.MirrorCS", {"start": v(169.63, -65.07) * mm, "end": v(182.86, -58.77) * mm});
            skLineSegment(sketch, "E631.MirrorCS", {"start": v(180.66, -90.55) * mm, "end": v(191.39, -80.57) * mm});
            skLineSegment(sketch, "E632.MirrorCS", {"start": v(223.32, -127.96) * mm, "end": v(225.75, -113.52) * mm});
            skLineSegment(sketch, "E633.MirrorCS", {"start": v(279.97, -132.18) * mm, "end": v(272.74, -119.41) * mm});
            skLineSegment(sketch, "E634.MirrorCS", {"start": v(235.14, -132.18) * mm, "end": v(242.37, -119.41) * mm});
            skLineSegment(sketch, "E635.MirrorCS", {"start": v(206.97, -118.85) * mm, "end": v(218.12, -109.34) * mm});
            skLineSegment(sketch, "E636.MirrorCS", {"start": v(291.78, -127.96) * mm, "end": v(289.36, -113.52) * mm});
            skLineSegment(sketch, "E637.MirrorCS", {"start": v(334.45, -90.55) * mm, "end": v(323.72, -80.57) * mm});
            skLineSegment(sketch, "E638.MirrorCS", {"start": v(251.07, -134.36) * mm, "end": v(248.64, -119.9) * mm});
            skLineSegment(sketch, "E639.MirrorCS", {"start": v(187.46, -101.09) * mm, "end": v(200.97, -95.37) * mm});
            skLineSegment(sketch, "E640.MirrorCS", {"start": v(263.61, -134.44) * mm, "end": v(266.27, -120.04) * mm});
            skLineSegment(sketch, "E641.MirrorCS", {"start": v(172.96, -77.17) * mm, "end": v(187.56, -75.77) * mm});
            skLineSegment(sketch, "E642.MirrorCS", {"start": v(308.14, -118.85) * mm, "end": v(296.99, -109.34) * mm});
            skArc(sketch, "E643.MirrorCS", {"start": v(189.94, -62) * mm, "mid": v(187.35, -58.02) * mm, "end": v(182.61, -58.43) * mm});
            skArc(sketch, "E644.MirrorCS", {"start": v(325.17, -62) * mm, "mid": v(327.96, -58.74) * mm, "end": v(332.25, -58.77) * mm});
            skPoint(sketch, "E645.visualSharp", {"position": v(-63.24, 139.93) * mm});
            skPoint(sketch, "E646.visualSharp", {"position": v(-56.56, 141.3) * mm});
            skArc(sketch, "E646.filletArc", {"start": v(-56.56, 141.34) * mm, "mid": v(-56.55, 141.3) * mm, "end": v(-56.55, 141.26) * mm});
            skLineSegment(sketch, "E647.MirrorCS", {"start": v(-70.93, -128.58) * mm, "end": v(-62.06, -133.76) * mm});
            skArc(sketch, "E648.MirrorCS", {"start": v(-70.7, 129.43) * mm, "mid": v(-74.94, 128.59) * mm, "end": v(-78.31, 131.29) * mm});
            skArc(sketch, "E649.MirrorCS", {"start": v(-62.52, 139.03) * mm, "mid": v(-62.4, 135.9) * mm, "end": v(-64.1, 133.27) * mm});
            skLineSegment(sketch, "E650.MirrorCS", {"start": v(-64.1, 133.27) * mm, "end": v(-70.7, 129.43) * mm});
            skSolve(sketch);
        }
        {
            var Q0;
            Q0=makeQuery(id+"F0.imprint","IMPRINT",FACE,{"disambiguationData":[TD([[makeQuery(id+"F0.imprint","IMPRINT",EDGE,{"derivedFrom":sQuery(id+"F0.wireOp",EDGE,"E178.MirrorCS")}),1.0]])]});
            var Q1;
            Q1=makeQuery(id+"F0.imprint","IMPRINT",FACE,{"disambiguationData":[TD([[makeQuery(id+"F0.imprint","IMPRINT",EDGE,{"derivedFrom":sQuery(id+"F0.wireOp",EDGE,"E202.MirrorCS")}),1.0]])]});
            var Q2;
            Q2=makeQuery(id+"F0.imprint","IMPRINT",FACE,{"disambiguationData":[TD([[makeQuery(id+"F0.imprint","IMPRINT",EDGE,{"derivedFrom":sQuery(id+"F0.wireOp",EDGE,"E267.MirrorCS")}),-1.0]])]});
            var Q3;
            {var subQ0=sQuery(id+"F0.wireOp",EDGE,"E213.MirrorCS");Q3=makeQuery(id+"F0.imprint","IMPRINT",FACE,{"disambiguationData":[TD([[makeQuery(id+"F0.imprint","IMPRINT",EDGE,{"derivedFrom":subQ0}),-1.0]])]});}
            var Q4;
            Q4=makeQuery(id+"F0.imprint","IMPRINT",FACE,{"disambiguationData":[TD([[makeQuery(id+"F0.imprint","IMPRINT",EDGE,{"derivedFrom":sQuery(id+"F0.wireOp",EDGE,"E60")}),-1.0]])]});
            var Q5;
            Q5=makeQuery(id+"F0.imprint","IMPRINT",FACE,{"disambiguationData":[TD([[makeQuery(id+"F0.imprint","IMPRINT",EDGE,{"derivedFrom":sQuery(id+"F0.wireOp",EDGE,"E68")}),-1.0]])]});
            var Q6;
            {var subQ4=sQuery(id+"F0.wireOp",EDGE,"E92.MirrorCS");Q6=makeQuery(id+"F0.imprint","IMPRINT",FACE,{"disambiguationData":[TD([[makeQuery(id+"F0.imprint","IMPRINT",EDGE,{"derivedFrom":subQ4}),-1.0]])]});}
            var Q7;
            Q7=makeQuery(id+"F0.imprint","IMPRINT",FACE,{"disambiguationData":[TD([[makeQuery(id+"F0.imprint","IMPRINT",EDGE,{"derivedFrom":sQuery(id+"F0.wireOp",EDGE,"E36")}),-1.0]])]});
            var Q8;
            {var subQ1=sQuery(id+"F0.wireOp",EDGE,"E195.MirrorCS");Q8=makeQuery(id+"F0.imprint","IMPRINT",FACE,{"disambiguationData":[TD([[makeQuery(id+"F0.imprint","IMPRINT",EDGE,{"derivedFrom":subQ1}),1.0]])]});}
            var Q9;
            Q9=makeQuery(id+"F0.imprint","IMPRINT",FACE,{"disambiguationData":[TD([[makeQuery(id+"F0.imprint","IMPRINT",EDGE,{"derivedFrom":sQuery(id+"F0.wireOp",EDGE,"E130.MirrorCS")}),1.0]])]});
            var Q10;
            Q10=makeQuery(id+"F0.imprint","IMPRINT",FACE,{"disambiguationData":[TD([[makeQuery(id+"F0.imprint","IMPRINT",EDGE,{"derivedFrom":sQuery(id+"F0.wireOp",EDGE,"E190.MirrorCS")}),1.0]])]});
            var Q11;
            Q11=makeQuery(id+"F0.imprint","IMPRINT",FACE,{"disambiguationData":[TD([[makeQuery(id+"F0.imprint","IMPRINT",EDGE,{"derivedFrom":sQuery(id+"F0.wireOp",EDGE,"E180.MirrorCS")}),1.0]])]});
            var Q12;
            Q12=makeQuery(id+"F0.imprint","IMPRINT",FACE,{"disambiguationData":[TD([[makeQuery(id+"F0.imprint","IMPRINT",EDGE,{"derivedFrom":sQuery(id+"F0.wireOp",EDGE,"E104.MirrorCS")}),-1.0]])]});
            var Q13;
            Q13=makeQuery(id+"F0.imprint","IMPRINT",FACE,{"disambiguationData":[TD([[makeQuery(id+"F0.imprint","IMPRINT",EDGE,{"derivedFrom":sQuery(id+"F0.wireOp",EDGE,"E52")}),-1.0]])]});
            var Q14;
            Q14=makeQuery(id+"F0.imprint","IMPRINT",FACE,{"disambiguationData":[TD([[makeQuery(id+"F0.imprint","IMPRINT",EDGE,{"derivedFrom":sQuery(id+"F0.wireOp",EDGE,"E118.MirrorCS")}),-1.0]])]});
            var Q15;
            Q15=makeQuery(id+"F0.imprint","IMPRINT",FACE,{"disambiguationData":[TD([[makeQuery(id+"F0.imprint","IMPRINT",EDGE,{"derivedFrom":sQuery(id+"F0.wireOp",EDGE,"E44")}),-1.0]])]});
            var Q16;
            Q16=makeQuery(id+"F0.imprint","IMPRINT",FACE,{"disambiguationData":[TD([[makeQuery(id+"F0.imprint","IMPRINT",EDGE,{"derivedFrom":sQuery(id+"F0.wireOp",EDGE,"E207.MirrorCS")}),1.0]])]});
            var Q17;
            Q17=makeQuery(id+"F0.imprint","IMPRINT",FACE,{"disambiguationData":[TD([[makeQuery(id+"F0.imprint","IMPRINT",EDGE,{"derivedFrom":sQuery(id+"F0.wireOp",EDGE,"E208.MirrorCS")}),1.0]])]});
            var Q18;
            {var subQ5=sQuery(id+"F0.wireOp",EDGE,"E227.MirrorCS");Q18=makeQuery(id+"F0.imprint","IMPRINT",FACE,{"disambiguationData":[TD([[makeQuery(id+"F0.imprint","IMPRINT",EDGE,{"derivedFrom":subQ5}),-1.0]])]});}
            var Q19;
            Q19=makeQuery(id+"F0.imprint","IMPRINT",FACE,{"disambiguationData":[TD([[makeQuery(id+"F0.imprint","IMPRINT",EDGE,{"derivedFrom":sQuery(id+"F0.wireOp",EDGE,"E176.MirrorCS")}),1.0]])]});
            var Q20;
            Q20=makeQuery(id+"F0.imprint","IMPRINT",FACE,{"disambiguationData":[TD([[makeQuery(id+"F0.imprint","IMPRINT",EDGE,{"derivedFrom":sQuery(id+"F0.wireOp",EDGE,"E134.MirrorCS")}),-1.0]])]});
            var Q21;
            {var subQ1=sQuery(id+"F0.wireOp",EDGE,"E237.MirrorCS");Q21=makeQuery(id+"F0.imprint","IMPRINT",FACE,{"disambiguationData":[TD([[makeQuery(id+"F0.imprint","IMPRINT",EDGE,{"derivedFrom":subQ1}),1.0]])]});}
            var Q22;
            Q22=makeQuery(id+"F0.imprint","IMPRINT",FACE,{"disambiguationData":[TD([[makeQuery(id+"F0.imprint","IMPRINT",EDGE,{"derivedFrom":sQuery(id+"F0.wireOp",EDGE,"E174.MirrorCS")}),1.0]])]});
            var Q23;
            {var subQ4=sQuery(id+"F0.wireOp",EDGE,"E119.MirrorCS");Q23=makeQuery(id+"F0.imprint","IMPRINT",FACE,{"disambiguationData":[TD([[makeQuery(id+"F0.imprint","IMPRINT",EDGE,{"derivedFrom":subQ4}),-1.0]])]});}
            var Q24;
            Q24=makeQuery(id+"F0.imprint","IMPRINT",FACE,{"disambiguationData":[TD([[makeQuery(id+"F0.imprint","IMPRINT",EDGE,{"derivedFrom":sQuery(id+"F0.wireOp",EDGE,"E20")}),-1.0]])]});
            var Q25;
            Q25=makeQuery(id+"F0.imprint","IMPRINT",FACE,{"disambiguationData":[TD([[makeQuery(id+"F0.imprint","IMPRINT",EDGE,{"derivedFrom":sQuery(id+"F0.wireOp",EDGE,"E28")}),-1.0]])]});
            var Q26;
            Q26=makeQuery(id+"F0.imprint","IMPRINT",FACE,{"disambiguationData":[TD([[makeQuery(id+"F0.imprint","IMPRINT",EDGE,{"derivedFrom":sQuery(id+"F0.wireOp",EDGE,"E12")}),-1.0]])]});
            var Q27;
            Q27=makeQuery(id+"F0.imprint","IMPRINT",FACE,{"disambiguationData":[TD([[makeQuery(id+"F0.imprint","IMPRINT",EDGE,{"derivedFrom":sQuery(id+"F0.wireOp",EDGE,"E55")}),1.0]])]});
            var Q28;
            Q28=makeQuery(id+"F0.imprint","IMPRINT",FACE,{"disambiguationData":[TD([[makeQuery(id+"F0.imprint","IMPRINT",EDGE,{"derivedFrom":sQuery(id+"F0.wireOp",EDGE,"E110.MirrorCS")}),1.0]])]});
            var Q29;
            Q29=makeQuery(id+"F0.imprint","IMPRINT",FACE,{"disambiguationData":[TD([[makeQuery(id+"F0.imprint","IMPRINT",EDGE,{"derivedFrom":sQuery(id+"F0.wireOp",EDGE,"E236.MirrorCS")}),1.0]])]});
            var Q30;
            Q30=makeQuery(id+"F0.imprint","IMPRINT",FACE,{"disambiguationData":[TD([[makeQuery(id+"F0.imprint","IMPRINT",EDGE,{"derivedFrom":sQuery(id+"F0.wireOp",EDGE,"E4")}),-1.0]])]});
            var Q31;
            Q31=makeQuery(id+"F0.imprint","IMPRINT",FACE,{"disambiguationData":[TD([[makeQuery(id+"F0.imprint","IMPRINT",EDGE,{"derivedFrom":sQuery(id+"F0.wireOp",EDGE,"E186.MirrorCS")}),1.0]])]});
            var Q32;
            Q32=makeQuery(id+"F0.imprint","IMPRINT",FACE,{"disambiguationData":[TD([[makeQuery(id+"F0.imprint","IMPRINT",EDGE,{"derivedFrom":sQuery(id+"F0.wireOp",EDGE,"E175.MirrorCS")}),1.0]])]});
            var Q33;
            Q33=makeQuery(id+"F0.imprint","IMPRINT",FACE,{"disambiguationData":[TD([[makeQuery(id+"F0.imprint","IMPRINT",EDGE,{"derivedFrom":sQuery(id+"F0.wireOp",EDGE,"E100.MirrorCS")}),-1.0]])]});
            var Q34;
            {var subQ5=sQuery(id+"F0.wireOp",EDGE,"E250.MirrorCS");Q34=makeQuery(id+"F0.imprint","IMPRINT",FACE,{"disambiguationData":[TD([[makeQuery(id+"F0.imprint","IMPRINT",EDGE,{"derivedFrom":subQ5}),-1.0]])]});}
            var Q35;
            Q35=makeQuery(id+"F0.imprint","IMPRINT",FACE,{"disambiguationData":[TD([[makeQuery(id+"F0.imprint","IMPRINT",EDGE,{"derivedFrom":sQuery(id+"F0.wireOp",EDGE,"E1")}),-1.0]])]});
            var Q36;
            {var subQ0=sQuery(id+"F0.wireOp",EDGE,"E274.MirrorCS");Q36=makeQuery(id+"F0.imprint","IMPRINT",FACE,{"disambiguationData":[TD([[makeQuery(id+"F0.imprint","IMPRINT",EDGE,{"derivedFrom":subQ0}),1.0]])]});}
            var Q37;
            {var subQ0=sQuery(id+"F0.wireOp",EDGE,"E276.MirrorCS");Q37=makeQuery(id+"F0.imprint","IMPRINT",FACE,{"disambiguationData":[TD([[makeQuery(id+"F0.imprint","IMPRINT",EDGE,{"derivedFrom":subQ0}),-1.0]])]});}
            var Q38;
            Q38=makeQuery(id+"F0.imprint","IMPRINT",FACE,{"disambiguationData":[TD([[makeQuery(id+"F0.imprint","IMPRINT",EDGE,{"derivedFrom":sQuery(id+"F0.wireOp",EDGE,"E275.MirrorCS")}),1.0]])]});
            var Q39;
            Q39=makeQuery(id+"F0.imprint","IMPRINT",FACE,{"disambiguationData":[TD([[makeQuery(id+"F0.imprint","IMPRINT",EDGE,{"derivedFrom":sQuery(id+"F0.wireOp",EDGE,"E241.MirrorCS")}),1.0]])]});
            var Q40;
            Q40=makeQuery(id+"F0.imprint","IMPRINT",FACE,{"disambiguationData":[TD([[makeQuery(id+"F0.imprint","IMPRINT",EDGE,{"derivedFrom":sQuery(id+"F0.wireOp",EDGE,"E129.MirrorCS")}),1.0]])]});
            var Q41;
            Q41=makeQuery(id+"F0.imprint","IMPRINT",FACE,{"disambiguationData":[TD([[makeQuery(id+"F0.imprint","IMPRINT",EDGE,{"derivedFrom":sQuery(id+"F0.wireOp",EDGE,"E138.MirrorCS")}),-1.0]])]});
            var Q42;
            {var subQ5=sQuery(id+"F0.wireOp",EDGE,"E245.MirrorCS");Q42=makeQuery(id+"F0.imprint","IMPRINT",FACE,{"disambiguationData":[TD([[makeQuery(id+"F0.imprint","IMPRINT",EDGE,{"derivedFrom":subQ5}),-1.0]])]});}
            var Q43;
            {var subQ6=sQuery(id+"F0.wireOp",EDGE,"E95.MirrorCS");Q43=makeQuery(id+"F0.imprint","IMPRINT",FACE,{"disambiguationData":[TD([[makeQuery(id+"F0.imprint","IMPRINT",EDGE,{"derivedFrom":subQ6}),-1.0]])]});}
            var Q44;
            {var subQ0=sQuery(id+"F0.wireOp",EDGE,"E31");Q44=makeQuery(id+"F0.imprint","IMPRINT",FACE,{"disambiguationData":[TD([[makeQuery(id+"F0.imprint","IMPRINT",EDGE,{"derivedFrom":subQ0}),1.0]])]});}
            var Q45;
            Q45=makeQuery(id+"F0.imprint","IMPRINT",FACE,{"disambiguationData":[TD([[makeQuery(id+"F0.imprint","IMPRINT",EDGE,{"derivedFrom":sQuery(id+"F0.wireOp",EDGE,"E15")}),1.0]])]});
            var Q46;
            {var subQ1=sQuery(id+"F0.wireOp",EDGE,"E79");Q46=makeQuery(id+"F0.imprint","IMPRINT",FACE,{"disambiguationData":[TD([[makeQuery(id+"F0.imprint","IMPRINT",EDGE,{"derivedFrom":subQ1}),1.0]])]});}
            var Q47;
            {var subQ5=sQuery(id+"F0.wireOp",EDGE,"E282.MirrorCS");Q47=makeQuery(id+"F0.imprint","IMPRINT",FACE,{"disambiguationData":[TD([[makeQuery(id+"F0.imprint","IMPRINT",EDGE,{"derivedFrom":subQ5}),1.0]])]});}
            var Q48;
            {var subQ1=sQuery(id+"F0.wireOp",EDGE,"E63");Q48=makeQuery(id+"F0.imprint","IMPRINT",FACE,{"disambiguationData":[TD([[makeQuery(id+"F0.imprint","IMPRINT",EDGE,{"derivedFrom":subQ1}),1.0]])]});}
            var Q49;
            Q49=makeQuery(id+"F0.imprint","IMPRINT",FACE,{"disambiguationData":[TD([[makeQuery(id+"F0.imprint","IMPRINT",EDGE,{"derivedFrom":sQuery(id+"F0.wireOp",EDGE,"E47")}),1.0]])]});
            var Q50;
            {var subQ5=sQuery(id+"F0.wireOp",EDGE,"E283.MirrorCS");Q50=makeQuery(id+"F0.imprint","IMPRINT",FACE,{"disambiguationData":[TD([[makeQuery(id+"F0.imprint","IMPRINT",EDGE,{"derivedFrom":subQ5}),1.0]])]});}
            var Q51;
            {var subQ5=sQuery(id+"F0.wireOp",EDGE,"E137.MirrorCS");Q51=makeQuery(id+"F0.imprint","IMPRINT",FACE,{"disambiguationData":[TD([[makeQuery(id+"F0.imprint","IMPRINT",EDGE,{"derivedFrom":subQ5}),-1.0]])]});}
            var Q52;
            {var subQ5=sQuery(id+"F0.wireOp",EDGE,"E226.MirrorCS");Q52=makeQuery(id+"F0.imprint","IMPRINT",FACE,{"disambiguationData":[TD([[makeQuery(id+"F0.imprint","IMPRINT",EDGE,{"derivedFrom":subQ5}),-1.0]])]});}
            var Q53;
            {var subQ5=sQuery(id+"F0.wireOp",EDGE,"E320.MirrorCS");Q53=makeQuery(id+"F0.imprint","IMPRINT",FACE,{"disambiguationData":[TD([[makeQuery(id+"F0.imprint","IMPRINT",EDGE,{"derivedFrom":subQ5}),1.0]])]});}
            var Q54;
            {var subQ5=sQuery(id+"F0.wireOp",EDGE,"E101.MirrorCS");Q54=makeQuery(id+"F0.imprint","IMPRINT",FACE,{"disambiguationData":[TD([[makeQuery(id+"F0.imprint","IMPRINT",EDGE,{"derivedFrom":subQ5}),-1.0]])]});}
            var Q55;
            {var subQ0=sQuery(id+"F0.wireOp",EDGE,"E193.MirrorCS");Q55=makeQuery(id+"F0.imprint","IMPRINT",FACE,{"disambiguationData":[TD([[makeQuery(id+"F0.imprint","IMPRINT",EDGE,{"derivedFrom":subQ0}),-1.0]])]});}
            var Q56;
            {var subQ5=sQuery(id+"F0.wireOp",EDGE,"E1798.MirrorCS");Q56=makeQuery(id+"F0.imprint","IMPRINT",FACE,{"disambiguationData":[TD([[makeQuery(id+"F0.imprint","IMPRINT",EDGE,{"derivedFrom":subQ5}),-1.0]])]});}
            var Q57;
            {var subQ5=sQuery(id+"F0.wireOp",EDGE,"E288.MirrorCS");Q57=makeQuery(id+"F0.imprint","IMPRINT",FACE,{"disambiguationData":[TD([[makeQuery(id+"F0.imprint","IMPRINT",EDGE,{"derivedFrom":subQ5}),1.0]])]});}
            var Q58;
            Q58=makeQuery(id+"F0.imprint","IMPRINT",FACE,{"disambiguationData":[TD([[makeQuery(id+"F0.imprint","IMPRINT",EDGE,{"derivedFrom":sQuery(id+"F0.wireOp",EDGE,"E7")}),1.0]])]});
            var Q59;
            {var subQ1=sQuery(id+"F0.wireOp",EDGE,"E124.MirrorCS");Q59=makeQuery(id+"F0.imprint","IMPRINT",FACE,{"disambiguationData":[TD([[makeQuery(id+"F0.imprint","IMPRINT",EDGE,{"derivedFrom":subQ1}),-1.0]])]});}
            var Q60;
            {var subQ5=sQuery(id+"F0.wireOp",EDGE,"E315.MirrorCS");Q60=makeQuery(id+"F0.imprint","IMPRINT",FACE,{"disambiguationData":[TD([[makeQuery(id+"F0.imprint","IMPRINT",EDGE,{"derivedFrom":subQ5}),1.0]])]});}
            var Q61;
            {var subQ5=sQuery(id+"F0.wireOp",EDGE,"E123.MirrorCS");Q61=makeQuery(id+"F0.imprint","IMPRINT",FACE,{"disambiguationData":[TD([[makeQuery(id+"F0.imprint","IMPRINT",EDGE,{"derivedFrom":subQ5}),-1.0]])]});}
            var Q62;
            {var subQ5=sQuery(id+"F0.wireOp",EDGE,"E87");Q62=makeQuery(id+"F0.imprint","IMPRINT",FACE,{"disambiguationData":[TD([[makeQuery(id+"F0.imprint","IMPRINT",EDGE,{"derivedFrom":subQ5}),1.0]])]});}
            var Q63;
            {var subQ5=sQuery(id+"F0.wireOp",EDGE,"E278.MirrorCS");Q63=makeQuery(id+"F0.imprint","IMPRINT",FACE,{"disambiguationData":[TD([[makeQuery(id+"F0.imprint","IMPRINT",EDGE,{"derivedFrom":subQ5}),1.0]])]});}
            var Q64;
            {var subQ5=sQuery(id+"F0.wireOp",EDGE,"E201.MirrorCS");Q64=makeQuery(id+"F0.imprint","IMPRINT",FACE,{"disambiguationData":[TD([[makeQuery(id+"F0.imprint","IMPRINT",EDGE,{"derivedFrom":subQ5}),-1.0]])]});}
            var Q65;
            Q65=makeQuery(id+"F0.imprint","IMPRINT",FACE,{"disambiguationData":[TD([[makeQuery(id+"F0.imprint","IMPRINT",EDGE,{"derivedFrom":sQuery(id+"F0.wireOp",EDGE,"E23")}),1.0]])]});
            var Q66;
            {var subQ5=sQuery(id+"F0.wireOp",EDGE,"E98.MirrorCS");Q66=makeQuery(id+"F0.imprint","IMPRINT",FACE,{"disambiguationData":[TD([[makeQuery(id+"F0.imprint","IMPRINT",EDGE,{"derivedFrom":subQ5}),-1.0]])]});}
            var Q67;
            Q67=makeQuery(id+"F0.imprint","IMPRINT",FACE,{"disambiguationData":[TD([[makeQuery(id+"F0.imprint","IMPRINT",EDGE,{"derivedFrom":sQuery(id+"F0.wireOp",EDGE,"E204.MirrorCS")}),-1.0]])]});
            var Q68;
            {var subQ5=sQuery(id+"F0.wireOp",EDGE,"E164.MirrorCS");Q68=makeQuery(id+"F0.imprint","IMPRINT",FACE,{"disambiguationData":[TD([[makeQuery(id+"F0.imprint","IMPRINT",EDGE,{"derivedFrom":subQ5}),-1.0]])]});}
            var Q69;
            {var subQ5=sQuery(id+"F0.wireOp",EDGE,"E114.MirrorCS");Q69=makeQuery(id+"F0.imprint","IMPRINT",FACE,{"disambiguationData":[TD([[makeQuery(id+"F0.imprint","IMPRINT",EDGE,{"derivedFrom":subQ5}),-1.0]])]});}
            var Q70;
            {var subQ5=sQuery(id+"F0.wireOp",EDGE,"E229.MirrorCS");Q70=makeQuery(id+"F0.imprint","IMPRINT",FACE,{"disambiguationData":[TD([[makeQuery(id+"F0.imprint","IMPRINT",EDGE,{"derivedFrom":subQ5}),-1.0]])]});}
            var Q71;
            {var subQ5=sQuery(id+"F0.wireOp",EDGE,"E314.MirrorCS");Q71=makeQuery(id+"F0.imprint","IMPRINT",FACE,{"disambiguationData":[TD([[makeQuery(id+"F0.imprint","IMPRINT",EDGE,{"derivedFrom":subQ5}),1.0]])]});}
            var Q72;
            Q72=makeQuery(id+"F0.imprint","IMPRINT",FACE,{"disambiguationData":[TD([[makeQuery(id+"F0.imprint","IMPRINT",EDGE,{"derivedFrom":sQuery(id+"F0.wireOp",EDGE,"E39")}),1.0]])]});
            var Q73;
            {var subQ5=sQuery(id+"F0.wireOp",EDGE,"E217.MirrorCS");Q73=makeQuery(id+"F0.imprint","IMPRINT",FACE,{"disambiguationData":[TD([[makeQuery(id+"F0.imprint","IMPRINT",EDGE,{"derivedFrom":subQ5}),1.0]])]});}
            var Q74;
            {var subQ1=sQuery(id+"F0.wireOp",EDGE,"E120.MirrorCS");Q74=makeQuery(id+"F0.imprint","IMPRINT",FACE,{"disambiguationData":[TD([[makeQuery(id+"F0.imprint","IMPRINT",EDGE,{"derivedFrom":subQ1}),-1.0]])]});}
            var Q75;
            {var subQ5=sQuery(id+"F0.wireOp",EDGE,"E71");Q75=makeQuery(id+"F0.imprint","IMPRINT",FACE,{"disambiguationData":[TD([[makeQuery(id+"F0.imprint","IMPRINT",EDGE,{"derivedFrom":subQ5}),1.0]])]});}
            var Q76;
            {var subQ5=sQuery(id+"F0.wireOp",EDGE,"E203.MirrorCS");Q76=makeQuery(id+"F0.imprint","IMPRINT",FACE,{"disambiguationData":[TD([[makeQuery(id+"F0.imprint","IMPRINT",EDGE,{"derivedFrom":subQ5}),-1.0]])]});}
            var Q77;
            {var subQ5=sQuery(id+"F0.wireOp",EDGE,"E277.MirrorCS");Q77=makeQuery(id+"F0.imprint","IMPRINT",FACE,{"disambiguationData":[TD([[makeQuery(id+"F0.imprint","IMPRINT",EDGE,{"derivedFrom":subQ5}),1.0]])]});}
            var Q78;
            Q78=makeQuery(id+"F0.imprint","IMPRINT",FACE,{"disambiguationData":[TD([[makeQuery(id+"F0.imprint","IMPRINT",EDGE,{"derivedFrom":sQuery(id+"F0.wireOp",EDGE,"E84")}),-1.0]])]});
            var Q79;
            Q79=makeQuery(id+"F0.imprint","IMPRINT",FACE,{"disambiguationData":[TD([[makeQuery(id+"F0.imprint","IMPRINT",EDGE,{"derivedFrom":sQuery(id+"F0.wireOp",EDGE,"E99.MirrorCS")}),1.0]])]});
            var Q80;
            Q80=makeQuery(id+"F0.imprint","IMPRINT",FACE,{"disambiguationData":[TD([[makeQuery(id+"F0.imprint","IMPRINT",EDGE,{"derivedFrom":sQuery(id+"F0.wireOp",EDGE,"E76")}),-1.0]])]});
            extrude(context, id + "F1", {"entities" : qUnion([Q0, Q1, Q2, Q3, Q4, Q5, Q6, Q7, Q8, Q9, Q10, Q11, Q12, Q13, Q14, Q15, Q16, Q17, Q18, Q19, Q20, Q21, Q22, Q23, Q24, Q25, Q26, Q27, Q28, Q29, Q30, Q31, Q32, Q33, Q34, Q35, Q36, Q37, Q38, Q39, Q40, Q41, Q42, Q43, Q44, Q45, Q46, Q47, Q48, Q49, Q50, Q51, Q52, Q53, Q54, Q55, Q56, Q57, Q58, Q59, Q60, Q61, Q62, Q63, Q64, Q65, Q66, Q67, Q68, Q69, Q70, Q71, Q72, Q73, Q74, Q75, Q76, Q77, Q78, Q79, Q80]), "depth" : 12.7 * mm});
        }
        {
            var Q0;
            Q0=makeQuery(id+"F0.imprint","IMPRINT",FACE,{"disambiguationData":[TD([[makeQuery(id+"F0.imprint","IMPRINT",EDGE,{"derivedFrom":sQuery(id+"F0.wireOp",EDGE,"E428.MirrorCS")}),-1.0]])]});
            var Q1;
            Q1=makeQuery(id+"F0.imprint","IMPRINT",FACE,{"disambiguationData":[TD([[makeQuery(id+"F0.imprint","IMPRINT",EDGE,{"derivedFrom":sQuery(id+"F0.wireOp",EDGE,"E3")}),-1.0]])]});
            var Q2;
            Q2=makeQuery(id+"F0.imprint","IMPRINT",FACE,{"disambiguationData":[TD([[makeQuery(id+"F0.imprint","IMPRINT",EDGE,{"derivedFrom":sQuery(id+"F0.wireOp",EDGE,"E417.MirrorCS")}),-1.0]])]});
            var Q3;
            Q3=makeQuery(id+"F0.imprint","IMPRINT",FACE,{"disambiguationData":[TD([[makeQuery(id+"F0.imprint","IMPRINT",EDGE,{"derivedFrom":sQuery(id+"F0.wireOp",EDGE,"E3")}),1.0]])]});
            var Q4;
            Q4=makeQuery(id+"F0.imprint","IMPRINT",FACE,{"disambiguationData":[TD([[makeQuery(id+"F0.imprint","IMPRINT",EDGE,{"derivedFrom":sQuery(id+"F0.wireOp",EDGE,"E390.MirrorCS")}),-1.0]])]});
            var Q5;
            Q5=makeQuery(id+"F0.imprint","IMPRINT",FACE,{"disambiguationData":[TD([[makeQuery(id+"F0.imprint","IMPRINT",EDGE,{"derivedFrom":sQuery(id+"F0.wireOp",EDGE,"E419.MirrorCS")}),-1.0]])]});
            var Q6;
            {var subQ4=sQuery(id+"F0.wireOp",EDGE,"E421.MirrorCS");Q6=makeQuery(id+"F0.imprint","IMPRINT",FACE,{"disambiguationData":[TD([[makeQuery(id+"F0.imprint","IMPRINT",EDGE,{"derivedFrom":subQ4}),-1.0]])]});}
            var Q7;
            Q7=makeQuery(id+"F0.imprint","IMPRINT",FACE,{"disambiguationData":[TD([[makeQuery(id+"F0.imprint","IMPRINT",EDGE,{"derivedFrom":sQuery(id+"F0.wireOp",EDGE,"E363")}),-1.0]])]});
            var Q8;
            Q8=makeQuery(id+"F0.imprint","IMPRINT",FACE,{"disambiguationData":[TD([[makeQuery(id+"F0.imprint","IMPRINT",EDGE,{"derivedFrom":sQuery(id+"F0.wireOp",EDGE,"E393.MirrorCS")}),1.0]])]});
            var Q9;
            Q9=makeQuery(id+"F0.imprint","IMPRINT",FACE,{"disambiguationData":[TD([[makeQuery(id+"F0.imprint","IMPRINT",EDGE,{"derivedFrom":sQuery(id+"F0.wireOp",EDGE,"E340")}),-1.0]])]});
            var Q10;
            Q10=makeQuery(id+"F0.imprint","IMPRINT",FACE,{"disambiguationData":[TD([[makeQuery(id+"F0.imprint","IMPRINT",EDGE,{"derivedFrom":sQuery(id+"F0.wireOp",EDGE,"E355")}),-1.0]])]});
            var Q11;
            Q11=makeQuery(id+"F0.imprint","IMPRINT",FACE,{"disambiguationData":[TD([[makeQuery(id+"F0.imprint","IMPRINT",EDGE,{"derivedFrom":sQuery(id+"F0.wireOp",EDGE,"E423.MirrorCS")}),-1.0]])]});
            var Q12;
            Q12=makeQuery(id+"F0.imprint","IMPRINT",FACE,{"disambiguationData":[TD([[makeQuery(id+"F0.imprint","IMPRINT",EDGE,{"derivedFrom":sQuery(id+"F0.wireOp",EDGE,"E332")}),-1.0]])]});
            var Q13;
            {var subQ5=sQuery(id+"F0.wireOp",EDGE,"E374.MirrorCS");Q13=makeQuery(id+"F0.imprint","IMPRINT",FACE,{"disambiguationData":[TD([[makeQuery(id+"F0.imprint","IMPRINT",EDGE,{"derivedFrom":subQ5}),-1.0]])]});}
            var Q14;
            Q14=makeQuery(id+"F0.imprint","IMPRINT",FACE,{"disambiguationData":[TD([[makeQuery(id+"F0.imprint","IMPRINT",EDGE,{"derivedFrom":sQuery(id+"F0.wireOp",EDGE,"E373.MirrorCS")}),-1.0]])]});
            var Q15;
            Q15=makeQuery(id+"F0.imprint","IMPRINT",FACE,{"disambiguationData":[TD([[makeQuery(id+"F0.imprint","IMPRINT",EDGE,{"derivedFrom":sQuery(id+"F0.wireOp",EDGE,"E422.MirrorCS")}),1.0]])]});
            var Q16;
            Q16=makeQuery(id+"F0.imprint","IMPRINT",FACE,{"disambiguationData":[TD([[makeQuery(id+"F0.imprint","IMPRINT",EDGE,{"derivedFrom":sQuery(id+"F0.wireOp",EDGE,"E420.MirrorCS")}),-1.0]])]});
            var Q17;
            Q17=makeQuery(id+"F0.imprint","IMPRINT",FACE,{"disambiguationData":[TD([[makeQuery(id+"F0.imprint","IMPRINT",EDGE,{"derivedFrom":sQuery(id+"F0.wireOp",EDGE,"E446.MirrorCS")}),-1.0]])]});
            var Q18;
            {var subQ6=sQuery(id+"F0.wireOp",EDGE,"E415.MirrorCS");Q18=makeQuery(id+"F0.imprint","IMPRINT",FACE,{"disambiguationData":[TD([[makeQuery(id+"F0.imprint","IMPRINT",EDGE,{"derivedFrom":subQ6}),-1.0]])]});}
            var Q19;
            {var subQ1=sQuery(id+"F0.wireOp",EDGE,"E382.MirrorCS");Q19=makeQuery(id+"F0.imprint","IMPRINT",FACE,{"disambiguationData":[TD([[makeQuery(id+"F0.imprint","IMPRINT",EDGE,{"derivedFrom":subQ1}),-1.0]])]});}
            var Q20;
            {var subQ5=sQuery(id+"F0.wireOp",EDGE,"E383.MirrorCS");Q20=makeQuery(id+"F0.imprint","IMPRINT",FACE,{"disambiguationData":[TD([[makeQuery(id+"F0.imprint","IMPRINT",EDGE,{"derivedFrom":subQ5}),-1.0]])]});}
            var Q21;
            {var subQ5=sQuery(id+"F0.wireOp",EDGE,"E327");Q21=makeQuery(id+"F0.imprint","IMPRINT",FACE,{"disambiguationData":[TD([[makeQuery(id+"F0.imprint","IMPRINT",EDGE,{"derivedFrom":subQ5}),1.0]])]});}
            var Q22;
            Q22=makeQuery(id+"F0.imprint","IMPRINT",FACE,{"disambiguationData":[TD([[makeQuery(id+"F0.imprint","IMPRINT",EDGE,{"derivedFrom":sQuery(id+"F0.wireOp",EDGE,"E335")}),1.0]])]});
            var Q23;
            {var subQ5=sQuery(id+"F0.wireOp",EDGE,"E378.MirrorCS");Q23=makeQuery(id+"F0.imprint","IMPRINT",FACE,{"disambiguationData":[TD([[makeQuery(id+"F0.imprint","IMPRINT",EDGE,{"derivedFrom":subQ5}),-1.0]])]});}
            var Q24;
            Q24=makeQuery(id+"F0.imprint","IMPRINT",FACE,{"disambiguationData":[TD([[makeQuery(id+"F0.imprint","IMPRINT",EDGE,{"derivedFrom":sQuery(id+"F0.wireOp",EDGE,"E324")}),-1.0]])]});
            var Q25;
            {var subQ1=sQuery(id+"F0.wireOp",EDGE,"E384.MirrorCS");Q25=makeQuery(id+"F0.imprint","IMPRINT",FACE,{"disambiguationData":[TD([[makeQuery(id+"F0.imprint","IMPRINT",EDGE,{"derivedFrom":subQ1}),-1.0]])]});}
            var Q26;
            {var subQ4=sQuery(id+"F0.wireOp",EDGE,"E372.MirrorCS");Q26=makeQuery(id+"F0.imprint","IMPRINT",FACE,{"disambiguationData":[TD([[makeQuery(id+"F0.imprint","IMPRINT",EDGE,{"derivedFrom":subQ4}),-1.0]])]});}
            var Q27;
            Q27=makeQuery(id+"F0.imprint","IMPRINT",FACE,{"disambiguationData":[TD([[makeQuery(id+"F0.imprint","IMPRINT",EDGE,{"derivedFrom":sQuery(id+"F0.wireOp",EDGE,"E445.MirrorCS")}),-1.0]])]});
            var Q28;
            {var subQ1=sQuery(id+"F0.wireOp",EDGE,"E416.MirrorCS");Q28=makeQuery(id+"F0.imprint","IMPRINT",FACE,{"disambiguationData":[TD([[makeQuery(id+"F0.imprint","IMPRINT",EDGE,{"derivedFrom":subQ1}),1.0]])]});}
            var Q29;
            {var subQ6=sQuery(id+"F0.wireOp",EDGE,"E350");Q29=makeQuery(id+"F0.imprint","IMPRINT",FACE,{"disambiguationData":[TD([[makeQuery(id+"F0.imprint","IMPRINT",EDGE,{"derivedFrom":subQ6}),1.0]])]});}
            var Q30;
            {var subQ0=sQuery(id+"F0.wireOp",EDGE,"E358");Q30=makeQuery(id+"F0.imprint","IMPRINT",FACE,{"disambiguationData":[TD([[makeQuery(id+"F0.imprint","IMPRINT",EDGE,{"derivedFrom":subQ0}),1.0]])]});}
            var Q31;
            Q31=makeQuery(id+"F0.imprint","IMPRINT",FACE,{"disambiguationData":[TD([[makeQuery(id+"F0.imprint","IMPRINT",EDGE,{"derivedFrom":sQuery(id+"F0.wireOp",EDGE,"979ec95b-2720-4346-9246-acc6462adfab")}),-1.0]])]});
            var Q32;
            {var subQ5=sQuery(id+"F0.wireOp",EDGE,"E343");Q32=makeQuery(id+"F0.imprint","IMPRINT",FACE,{"disambiguationData":[TD([[makeQuery(id+"F0.imprint","IMPRINT",EDGE,{"derivedFrom":subQ5}),1.0]])]});}
            var Q33;
            {var subQ5=sQuery(id+"F0.wireOp",EDGE,"E412.MirrorCS");Q33=makeQuery(id+"F0.imprint","IMPRINT",FACE,{"disambiguationData":[TD([[makeQuery(id+"F0.imprint","IMPRINT",EDGE,{"derivedFrom":subQ5}),1.0]])]});}
            var Q34;
            {var subQ4=sQuery(id+"F0.wireOp",EDGE,"E386.MirrorCS");Q34=makeQuery(id+"F0.imprint","IMPRINT",FACE,{"disambiguationData":[TD([[makeQuery(id+"F0.imprint","IMPRINT",EDGE,{"derivedFrom":subQ4}),-1.0]])]});}
            var Q35;
            {var subQ5=sQuery(id+"F0.wireOp",EDGE,"E436.MirrorCS");Q35=makeQuery(id+"F0.imprint","IMPRINT",FACE,{"disambiguationData":[TD([[makeQuery(id+"F0.imprint","IMPRINT",EDGE,{"derivedFrom":subQ5}),-1.0]])]});}
            var Q36;
            {var subQ5=sQuery(id+"F0.wireOp",EDGE,"E366");Q36=makeQuery(id+"F0.imprint","IMPRINT",FACE,{"disambiguationData":[TD([[makeQuery(id+"F0.imprint","IMPRINT",EDGE,{"derivedFrom":subQ5}),1.0]])]});}
            var Q37;
            {var subQ0=sQuery(id+"F0.wireOp",EDGE,"E448.MirrorCS");Q37=makeQuery(id+"F0.imprint","IMPRINT",FACE,{"disambiguationData":[TD([[makeQuery(id+"F0.imprint","IMPRINT",EDGE,{"derivedFrom":subQ0}),-1.0]])]});}
            var Q38;
            {var subQ1=sQuery(id+"F0.wireOp",EDGE,"E435.MirrorCS");Q38=makeQuery(id+"F0.imprint","IMPRINT",FACE,{"disambiguationData":[TD([[makeQuery(id+"F0.imprint","IMPRINT",EDGE,{"derivedFrom":subQ1}),1.0]])]});}
            var Q39;
            {var subQ5=sQuery(id+"F0.wireOp",EDGE,"E447.MirrorCS");Q39=makeQuery(id+"F0.imprint","IMPRINT",FACE,{"disambiguationData":[TD([[makeQuery(id+"F0.imprint","IMPRINT",EDGE,{"derivedFrom":subQ5}),-1.0]])]});}
            var Q40;
            {var subQ5=sQuery(id+"F0.wireOp",EDGE,"E429.MirrorCS");Q40=makeQuery(id+"F0.imprint","IMPRINT",FACE,{"disambiguationData":[TD([[makeQuery(id+"F0.imprint","IMPRINT",EDGE,{"derivedFrom":subQ5}),-1.0]])]});}
            var Q41;
            {var subQ5=sQuery(id+"F0.wireOp",EDGE,"E443.MirrorCS");Q41=makeQuery(id+"F0.imprint","IMPRINT",FACE,{"disambiguationData":[TD([[makeQuery(id+"F0.imprint","IMPRINT",EDGE,{"derivedFrom":subQ5}),1.0]])]});}
            var Q42;
            Q42=sQuery(id+"F0.wireOp",EDGE,"E333");
            var Q43;
            Q43=sQuery(id+"F0.wireOp",EDGE,"E337.filletArc");
            var Q44;
            Q44=sQuery(id+"F0.wireOp",EDGE,"E398.MirrorCS");
            var Q45;
            Q45=sQuery(id+"F0.wireOp",EDGE,"E377.MirrorCS");
            var Q46;
            Q46=sQuery(id+"F0.wireOp",EDGE,"E430.MirrorCS");
            var Q47;
            Q47=sQuery(id+"F0.wireOp",EDGE,"E453.MirrorCS");
            var Q48;
            Q48=sQuery(id+"F0.wireOp",EDGE,"E479.MirrorCS");
            var Q49;
            Q49=sQuery(id+"F0.wireOp",EDGE,"E462.MirrorCS");
            var Q50;
            Q50=sQuery(id+"F0.wireOp",EDGE,"E459.MirrorCS");
            var Q51;
            Q51=sQuery(id+"F0.wireOp",EDGE,"E446.MirrorCS");
            var Q52;
            Q52=sQuery(id+"F0.wireOp",EDGE,"E468.MirrorCS");
            var Q53;
            Q53=sQuery(id+"F0.wireOp",EDGE,"E336.filletArc");
            var Q54;
            Q54=sQuery(id+"F0.wireOp",EDGE,"E427.MirrorCS");
            var Q55;
            Q55=sQuery(id+"F0.wireOp",EDGE,"E383.MirrorCS");
            var Q56;
            Q56=sQuery(id+"F0.wireOp",EDGE,"E412.MirrorCS");
            var Q57;
            Q57=sQuery(id+"F0.wireOp",EDGE,"E410.MirrorCS");
            var Q58;
            Q58=sQuery(id+"F0.wireOp",EDGE,"E470.MirrorCS");
            var Q59;
            Q59=sQuery(id+"F0.wireOp",EDGE,"E332");
            var Q60;
            Q60=sQuery(id+"F0.wireOp",EDGE,"E416.MirrorCS");
            var Q61;
            Q61=sQuery(id+"F0.wireOp",EDGE,"E429.MirrorCS");
            var Q62;
            Q62=sQuery(id+"F0.wireOp",EDGE,"E417.MirrorCS");
            var Q63;
            Q63=sQuery(id+"F0.wireOp",EDGE,"E419.MirrorCS");
            var Q64;
            Q64=sQuery(id+"F0.wireOp",EDGE,"E3");
            var Q65;
            Q65=sQuery(id+"F0.wireOp",EDGE,"E464.MirrorCS");
            var Q66;
            Q66=sQuery(id+"F0.wireOp",EDGE,"E334");
            var Q67;
            Q67=sQuery(id+"F0.wireOp",EDGE,"E2");
            var Q68;
            Q68=sQuery(id+"F0.wireOp",EDGE,"E439.MirrorCS");
            var Q69;
            Q69=sQuery(id+"F0.wireOp",EDGE,"E450.MirrorCS");
            var Q70;
            Q70=sQuery(id+"F0.wireOp",EDGE,"E457.MirrorCS");
            var Q71;
            Q71=sQuery(id+"F0.wireOp",EDGE,"E454.MirrorCS");
            var Q72;
            Q72=sQuery(id+"F0.wireOp",EDGE,"E467.MirrorCS");
            var Q73;
            Q73=sQuery(id+"F0.wireOp",EDGE,"E372.MirrorCS");
            var Q74;
            Q74=sQuery(id+"F0.wireOp",EDGE,"E434.MirrorCS");
            var Q75;
            Q75=sQuery(id+"F0.wireOp",EDGE,"E461.MirrorCS");
            var Q76;
            Q76=sQuery(id+"F0.wireOp",EDGE,"E460.MirrorCS");
            var Q77;
            Q77=sQuery(id+"F0.wireOp",EDGE,"E442.MirrorCS");
            var Q78;
            Q78=sQuery(id+"F0.wireOp",EDGE,"E465.MirrorCS");
            var Q79;
            Q79=sQuery(id+"F0.wireOp",EDGE,"E472.MirrorCS");
            var Q80;
            Q80=sQuery(id+"F0.wireOp",EDGE,"E444.MirrorCS");
            var Q81;
            Q81=sQuery(id+"F0.wireOp",EDGE,"E343");
            var Q82;
            Q82=sQuery(id+"F0.wireOp",EDGE,"E393.MirrorCS");
            var Q83;
            Q83=sQuery(id+"F0.wireOp",EDGE,"E408.MirrorCS");
            var Q84;
            Q84=sQuery(id+"F0.wireOp",EDGE,"E395.MirrorCS");
            var Q85;
            Q85=sQuery(id+"F0.wireOp",EDGE,"E381.MirrorCS");
            var Q86;
            Q86=sQuery(id+"F0.wireOp",EDGE,"E481.MirrorCS");
            var Q87;
            Q87=sQuery(id+"F0.wireOp",EDGE,"E397.MirrorCS");
            var Q88;
            Q88=sQuery(id+"F0.wireOp",EDGE,"E407.MirrorCS");
            var Q89;
            Q89=sQuery(id+"F0.wireOp",EDGE,"E449.MirrorCS");
            var Q90;
            Q90=sQuery(id+"F0.wireOp",EDGE,"E476.MirrorCS");
            var Q91;
            Q91=sQuery(id+"F0.wireOp",EDGE,"E414.MirrorCS");
            var Q92;
            Q92=sQuery(id+"F0.wireOp",EDGE,"E475.MirrorCS");
            var Q93;
            Q93=sQuery(id+"F0.wireOp",EDGE,"E375.MirrorCS");
            var Q94;
            Q94=sQuery(id+"F0.wireOp",EDGE,"E435.MirrorCS");
            var Q95;
            Q95=sQuery(id+"F0.wireOp",EDGE,"E379.MirrorCS");
            var Q96;
            Q96=sQuery(id+"F0.wireOp",EDGE,"E387.MirrorCS");
            var Q97;
            Q97=sQuery(id+"F0.wireOp",EDGE,"E403.MirrorCS");
            var Q98;
            Q98=sQuery(id+"F0.wireOp",EDGE,"E356");
            var Q99;
            Q99=sQuery(id+"F0.wireOp",EDGE,"E480.MirrorCS");
            var Q100;
            Q100=sQuery(id+"F0.wireOp",EDGE,"E351.filletArc");
            var Q101;
            Q101=sQuery(id+"F0.wireOp",EDGE,"E359.filletArc");
            var Q102;
            Q102=sQuery(id+"F0.wireOp",EDGE,"E338.filletArc");
            var Q103;
            Q103=sQuery(id+"F0.wireOp",EDGE,"E367.filletArc");
            var Q104;
            Q104=sQuery(id+"F0.wireOp",EDGE,"E376.MirrorCS");
            var Q105;
            Q105=sQuery(id+"F0.wireOp",EDGE,"E390.MirrorCS");
            var Q106;
            Q106=sQuery(id+"F0.wireOp",EDGE,"E360.filletArc");
            var Q107;
            Q107=sQuery(id+"F0.wireOp",EDGE,"E384.MirrorCS");
            var Q108;
            Q108=sQuery(id+"F0.wireOp",EDGE,"E400.MirrorCS");
            var Q109;
            Q109=sQuery(id+"F0.wireOp",EDGE,"E382.MirrorCS");
            var Q110;
            Q110=sQuery(id+"F0.wireOp",EDGE,"E335");
            var Q111;
            Q111=sQuery(id+"F0.wireOp",EDGE,"E399.MirrorCS");
            var Q112;
            Q112=sQuery(id+"F0.wireOp",EDGE,"E385.MirrorCS");
            var Q113;
            Q113=sQuery(id+"F0.wireOp",EDGE,"E477.MirrorCS");
            var Q114;
            Q114=sQuery(id+"F0.wireOp",EDGE,"E357");
            var Q115;
            Q115=sQuery(id+"F0.wireOp",EDGE,"E478.MirrorCS");
            var Q116;
            Q116=sQuery(id+"F0.wireOp",EDGE,"E392.MirrorCS");
            var Q117;
            Q117=sQuery(id+"F0.wireOp",EDGE,"E352.filletArc");
            var Q118;
            Q118=sQuery(id+"F0.wireOp",EDGE,"E471.MirrorCS");
            var Q119;
            Q119=sQuery(id+"F0.wireOp",EDGE,"E466.MirrorCS");
            var Q120;
            Q120=sQuery(id+"F0.wireOp",EDGE,"E448.MirrorCS");
            var Q121;
            Q121=sQuery(id+"F0.wireOp",EDGE,"E380.MirrorCS");
            var Q122;
            Q122=sQuery(id+"F0.wireOp",EDGE,"E415.MirrorCS");
            var Q123;
            Q123=sQuery(id+"F0.wireOp",EDGE,"E371.MirrorCS");
            var Q124;
            Q124=sQuery(id+"F0.wireOp",EDGE,"E463.MirrorCS");
            var Q125;
            Q125=sQuery(id+"F0.wireOp",EDGE,"E404.MirrorCS");
            var Q126;
            Q126=sQuery(id+"F0.wireOp",EDGE,"E437.MirrorCS");
            var Q127;
            Q127=sQuery(id+"F0.wireOp",EDGE,"E469.MirrorCS");
            var Q128;
            Q128=sQuery(id+"F0.wireOp",EDGE,"E413.MirrorCS");
            var Q129;
            Q129=sQuery(id+"F0.wireOp",EDGE,"979ec95b-2720-4346-9246-acc6462adfab");
            var Q130;
            Q130=sQuery(id+"F0.wireOp",EDGE,"E389.MirrorCS");
            var Q131;
            Q131=sQuery(id+"F0.wireOp",EDGE,"E436.MirrorCS");
            var Q132;
            Q132=sQuery(id+"F0.wireOp",EDGE,"E425.MirrorCS");
            var Q133;
            Q133=sQuery(id+"F0.wireOp",EDGE,"E411.MirrorCS");
            var Q134;
            Q134=sQuery(id+"F0.wireOp",EDGE,"E368.filletArc");
            var Q135;
            Q135=sQuery(id+"F0.wireOp",EDGE,"E418.MirrorCS");
            var Q136;
            Q136=sQuery(id+"F0.wireOp",EDGE,"E406.MirrorCS");
            var Q137;
            Q137=sQuery(id+"F0.wireOp",EDGE,"E374.MirrorCS");
            var Q138;
            Q138=sQuery(id+"F0.wireOp",EDGE,"E443.MirrorCS");
            var Q139;
            Q139=sQuery(id+"F0.wireOp",EDGE,"E363");
            var Q140;
            Q140=sQuery(id+"F0.wireOp",EDGE,"E447.MirrorCS");
            var Q141;
            Q141=sQuery(id+"F0.wireOp",EDGE,"E365");
            var Q142;
            Q142=sQuery(id+"F0.wireOp",EDGE,"E474.MirrorCS");
            var Q143;
            Q143=sQuery(id+"F0.wireOp",EDGE,"E349");
            var Q144;
            Q144=sQuery(id+"F0.wireOp",EDGE,"E373.MirrorCS");
            var Q145;
            Q145=sQuery(id+"F0.wireOp",EDGE,"E405.MirrorCS");
            var Q146;
            Q146=sQuery(id+"F0.wireOp",EDGE,"E402.MirrorCS");
            var Q147;
            Q147=sQuery(id+"F0.wireOp",EDGE,"E401.MirrorCS");
            var Q148;
            Q148=sQuery(id+"F0.wireOp",EDGE,"E396.MirrorCS");
            var Q149;
            Q149=sQuery(id+"F0.wireOp",EDGE,"E364");
            var Q150;
            Q150=sQuery(id+"F0.wireOp",EDGE,"E366");
            var Q151;
            Q151=sQuery(id+"F0.wireOp",EDGE,"E370.filletArc");
            var Q152;
            Q152=sQuery(id+"F0.wireOp",EDGE,"E345.filletArc");
            var Q153;
            Q153=sQuery(id+"F0.wireOp",EDGE,"E378.MirrorCS");
            var Q154;
            Q154=sQuery(id+"F0.wireOp",EDGE,"E426.MirrorCS");
            var Q155;
            Q155=sQuery(id+"F0.wireOp",EDGE,"E362.filletArc");
            var Q156;
            Q156=sQuery(id+"F0.wireOp",EDGE,"E342");
            var Q157;
            Q157=sQuery(id+"F0.wireOp",EDGE,"E344.filletArc");
            var Q158;
            Q158=sQuery(id+"F0.wireOp",EDGE,"E440.MirrorCS");
            var Q159;
            Q159=sQuery(id+"F0.wireOp",EDGE,"E441.MirrorCS");
            var Q160;
            Q160=sQuery(id+"F0.wireOp",EDGE,"E354.filletArc");
            var Q161;
            Q161=sQuery(id+"F0.wireOp",EDGE,"E455.MirrorCS");
            var Q162;
            Q162=sQuery(id+"F0.wireOp",EDGE,"E421.MirrorCS");
            var Q163;
            Q163=sQuery(id+"F0.wireOp",EDGE,"E428.MirrorCS");
            var Q164;
            Q164=sQuery(id+"F0.wireOp",EDGE,"E452.MirrorCS");
            var Q165;
            Q165=sQuery(id+"F0.wireOp",EDGE,"E424.MirrorCS");
            var Q166;
            Q166=sQuery(id+"F0.wireOp",EDGE,"E451.MirrorCS");
            var Q167;
            Q167=sQuery(id+"F0.wireOp",EDGE,"E433.MirrorCS");
            var Q168;
            Q168=sQuery(id+"F0.wireOp",EDGE,"E348");
            var Q169;
            Q169=sQuery(id+"F0.wireOp",EDGE,"E346.filletArc");
            var Q170;
            Q170=sQuery(id+"F0.wireOp",EDGE,"E386.MirrorCS");
            var Q171;
            Q171=sQuery(id+"F0.wireOp",EDGE,"E420.MirrorCS");
            var Q172;
            Q172=sQuery(id+"F0.wireOp",EDGE,"E432.MirrorCS");
            var Q173;
            Q173=sQuery(id+"F0.wireOp",EDGE,"E409.MirrorCS");
            var Q174;
            Q174=sQuery(id+"F0.wireOp",EDGE,"E438.MirrorCS");
            var Q175;
            Q175=sQuery(id+"F0.wireOp",EDGE,"E369.filletArc");
            var Q176;
            Q176=sQuery(id+"F0.wireOp",EDGE,"E339.filletArc");
            var Q177;
            Q177=sQuery(id+"F0.wireOp",EDGE,"E458.MirrorCS");
            var Q178;
            Q178=sQuery(id+"F0.wireOp",EDGE,"E423.MirrorCS");
            var Q179;
            Q179=sQuery(id+"F0.wireOp",EDGE,"E350");
            var Q180;
            Q180=sQuery(id+"F0.wireOp",EDGE,"E388.MirrorCS");
            var Q181;
            Q181=sQuery(id+"F0.wireOp",EDGE,"E391.MirrorCS");
            var Q182;
            Q182=sQuery(id+"F0.wireOp",EDGE,"E355");
            var Q183;
            Q183=sQuery(id+"F0.wireOp",EDGE,"E394.MirrorCS");
            var Q184;
            Q184=sQuery(id+"F0.wireOp",EDGE,"E431.MirrorCS");
            var Q185;
            Q185=sQuery(id+"F0.wireOp",EDGE,"E473.MirrorCS");
            var Q186;
            Q186=sQuery(id+"F0.wireOp",EDGE,"E456.MirrorCS");
            var Q187;
            Q187=sQuery(id+"F0.wireOp",EDGE,"E482.MirrorCS");
            var Q188;
            Q188=sQuery(id+"F0.wireOp",EDGE,"E341");
            var Q189;
            Q189=sQuery(id+"F0.wireOp",EDGE,"E361.filletArc");
            var Q190;
            Q190=sQuery(id+"F0.wireOp",EDGE,"E340");
            var Q191;
            Q191=sQuery(id+"F0.wireOp",EDGE,"E445.MirrorCS");
            var Q192;
            Q192=sQuery(id+"F0.wireOp",EDGE,"E422.MirrorCS");
            var Q193;
            Q193=sQuery(id+"F0.wireOp",EDGE,"E358");
            var Q194;
            Q194=sQuery(id+"F0.wireOp",EDGE,"E347.filletArc");
            var Q195;
            Q195=sQuery(id+"F0.wireOp",EDGE,"E326");
            var Q196;
            Q196=sQuery(id+"F0.wireOp",EDGE,"E330.filletArc");
            var Q197;
            Q197=sQuery(id+"F0.wireOp",EDGE,"E325");
            var Q198;
            Q198=sQuery(id+"F0.wireOp",EDGE,"E329.filletArc");
            var Q199;
            Q199=sQuery(id+"F0.wireOp",EDGE,"E327");
            var Q200;
            Q200=sQuery(id+"F0.wireOp",EDGE,"E328.filletArc");
            var Q201;
            Q201=sQuery(id+"F0.wireOp",EDGE,"E353.filletArc");
            var Q202;
            Q202=sQuery(id+"F0.wireOp",EDGE,"E331.filletArc");
            var Q203;
            Q203=sQuery(id+"F0.wireOp",EDGE,"E324");
            extrude(context, id + "F2", {"entities" : qUnion([Q0, Q1, Q2, Q3, Q4, Q5, Q6, Q7, Q8, Q9, Q10, Q11, Q12, Q13, Q14, Q15, Q16, Q17, Q18, Q19, Q20, Q21, Q22, Q23, Q24, Q25, Q26, Q27, Q28, Q29, Q30, Q31, Q32, Q33, Q34, Q35, Q36, Q37, Q38, Q39, Q40, Q41]), "surfaceEntities" : qUnion([Q42, Q43, Q44, Q45, Q46, Q47, Q48, Q49, Q50, Q51, Q52, Q53, Q54, Q55, Q56, Q57, Q58, Q59, Q60, Q61, Q62, Q63, Q64, Q65, Q66, Q67, Q68, Q69, Q70, Q71, Q72, Q73, Q74, Q75, Q76, Q77, Q78, Q79, Q80, Q81, Q82, Q83, Q84, Q85, Q86, Q87, Q88, Q89, Q90, Q91, Q92, Q93, Q94, Q95, Q96, Q97, Q98, Q99, Q100, Q101, Q102, Q103, Q104, Q105, Q106, Q107, Q108, Q109, Q110, Q111, Q112, Q113, Q114, Q115, Q116, Q117, Q118, Q119, Q120, Q121, Q122, Q123, Q124, Q125, Q126, Q127, Q128, Q129, Q130, Q131, Q132, Q133, Q134, Q135, Q136, Q137, Q138, Q139, Q140, Q141, Q142, Q143, Q144, Q145, Q146, Q147, Q148, Q149, Q150, Q151, Q152, Q153, Q154, Q155, Q156, Q157, Q158, Q159, Q160, Q161, Q162, Q163, Q164, Q165, Q166, Q167, Q168, Q169, Q170, Q171, Q172, Q173, Q174, Q175, Q176, Q177, Q178, Q179, Q180, Q181, Q182, Q183, Q184, Q185, Q186, Q187, Q188, Q189, Q190, Q191, Q192, Q193, Q194, Q195, Q196, Q197, Q198, Q199, Q200, Q201, Q202, Q203]), "depth" : 6.35 * mm});
        }
        {
            var Q0;
            Q0=makeQuery(id+"F0.imprint","IMPRINT",FACE,{"disambiguationData":[TD([[makeQuery(id+"F0.imprint","IMPRINT",EDGE,{"derivedFrom":sQuery(id+"F0.wireOp",EDGE,"E555.MirrorCS")}),1.0]])]});
            var Q1;
            {var subQ1=sQuery(id+"F0.wireOp",EDGE,"E544.MirrorCS");Q1=makeQuery(id+"F0.imprint","IMPRINT",FACE,{"disambiguationData":[TD([[makeQuery(id+"F0.imprint","IMPRINT",EDGE,{"derivedFrom":subQ1}),-1.0]])]});}
            var Q2;
            Q2=makeQuery(id+"F0.imprint","IMPRINT",FACE,{"disambiguationData":[TD([[makeQuery(id+"F0.imprint","IMPRINT",EDGE,{"derivedFrom":sQuery(id+"F0.wireOp",EDGE,"E484")}),-1.0]])]});
            var Q3;
            Q3=makeQuery(id+"F0.imprint","IMPRINT",FACE,{"disambiguationData":[TD([[makeQuery(id+"F0.imprint","IMPRINT",EDGE,{"derivedFrom":sQuery(id+"F0.wireOp",EDGE,"E552.MirrorCS")}),-1.0]])]});
            var Q4;
            {var subQ5=sQuery(id+"F0.wireOp",EDGE,"E545.MirrorCS");Q4=makeQuery(id+"F0.imprint","IMPRINT",FACE,{"disambiguationData":[TD([[makeQuery(id+"F0.imprint","IMPRINT",EDGE,{"derivedFrom":subQ5}),-1.0]])]});}
            var Q5;
            {var subQ4=sQuery(id+"F0.wireOp",EDGE,"E534.MirrorCS");Q5=makeQuery(id+"F0.imprint","IMPRINT",FACE,{"disambiguationData":[TD([[makeQuery(id+"F0.imprint","IMPRINT",EDGE,{"derivedFrom":subQ4}),-1.0]])]});}
            var Q6;
            {var subQ0=sQuery(id+"F0.wireOp",EDGE,"E536.MirrorCS");Q6=makeQuery(id+"F0.imprint","IMPRINT",FACE,{"disambiguationData":[TD([[makeQuery(id+"F0.imprint","IMPRINT",EDGE,{"derivedFrom":subQ0}),-1.0]])]});}
            var Q7;
            {var subQ1=sQuery(id+"F0.wireOp",EDGE,"E546.MirrorCS");Q7=makeQuery(id+"F0.imprint","IMPRINT",FACE,{"disambiguationData":[TD([[makeQuery(id+"F0.imprint","IMPRINT",EDGE,{"derivedFrom":subQ1}),-1.0]])]});}
            var Q8;
            Q8=makeQuery(id+"F0.imprint","IMPRINT",FACE,{"disambiguationData":[TD([[makeQuery(id+"F0.imprint","IMPRINT",EDGE,{"derivedFrom":sQuery(id+"F0.wireOp",EDGE,"E579.MirrorCS")}),-1.0]])]});
            var Q9;
            {var subQ5=sQuery(id+"F0.wireOp",EDGE,"E605.MirrorCS");Q9=makeQuery(id+"F0.imprint","IMPRINT",FACE,{"disambiguationData":[TD([[makeQuery(id+"F0.imprint","IMPRINT",EDGE,{"derivedFrom":subQ5}),1.0]])]});}
            var Q10;
            Q10=makeQuery(id+"F0.imprint","IMPRINT",FACE,{"disambiguationData":[TD([[makeQuery(id+"F0.imprint","IMPRINT",EDGE,{"derivedFrom":sQuery(id+"F0.wireOp",EDGE,"E584.MirrorCS")}),1.0]])]});
            var Q11;
            {var subQ1=sQuery(id+"F0.wireOp",EDGE,"E578.MirrorCS");Q11=makeQuery(id+"F0.imprint","IMPRINT",FACE,{"disambiguationData":[TD([[makeQuery(id+"F0.imprint","IMPRINT",EDGE,{"derivedFrom":subQ1}),1.0]])]});}
            var Q12;
            Q12=makeQuery(id+"F0.imprint","IMPRINT",FACE,{"disambiguationData":[TD([[makeQuery(id+"F0.imprint","IMPRINT",EDGE,{"derivedFrom":sQuery(id+"F0.wireOp",EDGE,"E581.MirrorCS")}),-1.0]])]});
            var Q13;
            Q13=makeQuery(id+"F0.imprint","IMPRINT",FACE,{"disambiguationData":[TD([[makeQuery(id+"F0.imprint","IMPRINT",EDGE,{"derivedFrom":sQuery(id+"F0.wireOp",EDGE,"E585.MirrorCS")}),-1.0]])]});
            var Q14;
            {var subQ1=sQuery(id+"F0.wireOp",EDGE,"E597.MirrorCS");Q14=makeQuery(id+"F0.imprint","IMPRINT",FACE,{"disambiguationData":[TD([[makeQuery(id+"F0.imprint","IMPRINT",EDGE,{"derivedFrom":subQ1}),1.0]])]});}
            var Q15;
            {var subQ5=sQuery(id+"F0.wireOp",EDGE,"E574.MirrorCS");Q15=makeQuery(id+"F0.imprint","IMPRINT",FACE,{"disambiguationData":[TD([[makeQuery(id+"F0.imprint","IMPRINT",EDGE,{"derivedFrom":subQ5}),1.0]])]});}
            var Q16;
            Q16=makeQuery(id+"F0.imprint","IMPRINT",FACE,{"disambiguationData":[TD([[makeQuery(id+"F0.imprint","IMPRINT",EDGE,{"derivedFrom":sQuery(id+"F0.wireOp",EDGE,"E590.MirrorCS")}),-1.0]])]});
            var Q17;
            {var subQ5=sQuery(id+"F0.wireOp",EDGE,"E598.MirrorCS");Q17=makeQuery(id+"F0.imprint","IMPRINT",FACE,{"disambiguationData":[TD([[makeQuery(id+"F0.imprint","IMPRINT",EDGE,{"derivedFrom":subQ5}),-1.0]])]});}
            var Q18;
            Q18=makeQuery(id+"F0.imprint","IMPRINT",FACE,{"disambiguationData":[TD([[makeQuery(id+"F0.imprint","IMPRINT",EDGE,{"derivedFrom":sQuery(id+"F0.wireOp",EDGE,"E582.MirrorCS")}),-1.0]])]});
            var Q19;
            {var subQ5=sQuery(id+"F0.wireOp",EDGE,"E591.MirrorCS");Q19=makeQuery(id+"F0.imprint","IMPRINT",FACE,{"disambiguationData":[TD([[makeQuery(id+"F0.imprint","IMPRINT",EDGE,{"derivedFrom":subQ5}),-1.0]])]});}
            var Q20;
            Q20=makeQuery(id+"F0.imprint","IMPRINT",FACE,{"disambiguationData":[TD([[makeQuery(id+"F0.imprint","IMPRINT",EDGE,{"derivedFrom":sQuery(id+"F0.wireOp",EDGE,"E607.MirrorCS")}),-1.0]])]});
            var Q21;
            {var subQ0=sQuery(id+"F0.wireOp",EDGE,"E610.MirrorCS");Q21=makeQuery(id+"F0.imprint","IMPRINT",FACE,{"disambiguationData":[TD([[makeQuery(id+"F0.imprint","IMPRINT",EDGE,{"derivedFrom":subQ0}),-1.0]])]});}
            var Q22;
            {var subQ4=sQuery(id+"F0.wireOp",EDGE,"E583.MirrorCS");Q22=makeQuery(id+"F0.imprint","IMPRINT",FACE,{"disambiguationData":[TD([[makeQuery(id+"F0.imprint","IMPRINT",EDGE,{"derivedFrom":subQ4}),-1.0]])]});}
            var Q23;
            {var subQ4=sQuery(id+"F0.wireOp",EDGE,"E577.MirrorCS");Q23=makeQuery(id+"F0.imprint","IMPRINT",FACE,{"disambiguationData":[TD([[makeQuery(id+"F0.imprint","IMPRINT",EDGE,{"derivedFrom":subQ4}),-1.0]])]});}
            var Q24;
            Q24=makeQuery(id+"F0.imprint","IMPRINT",FACE,{"disambiguationData":[TD([[makeQuery(id+"F0.imprint","IMPRINT",EDGE,{"derivedFrom":sQuery(id+"F0.wireOp",EDGE,"E608.MirrorCS")}),-1.0]])]});
            var Q25;
            {var subQ5=sQuery(id+"F0.wireOp",EDGE,"E609.MirrorCS");Q25=makeQuery(id+"F0.imprint","IMPRINT",FACE,{"disambiguationData":[TD([[makeQuery(id+"F0.imprint","IMPRINT",EDGE,{"derivedFrom":subQ5}),-1.0]])]});}
            var Q26;
            Q26=makeQuery(id+"F0.imprint","IMPRINT",FACE,{"disambiguationData":[TD([[makeQuery(id+"F0.imprint","IMPRINT",EDGE,{"derivedFrom":sQuery(id+"F0.wireOp",EDGE,"E493")}),-1.0]])]});
            var Q27;
            Q27=makeQuery(id+"F0.imprint","IMPRINT",FACE,{"disambiguationData":[TD([[makeQuery(id+"F0.imprint","IMPRINT",EDGE,{"derivedFrom":sQuery(id+"F0.wireOp",EDGE,"E525")}),-1.0]])]});
            var Q28;
            {var subQ5=sQuery(id+"F0.wireOp",EDGE,"E528");Q28=makeQuery(id+"F0.imprint","IMPRINT",FACE,{"disambiguationData":[TD([[makeQuery(id+"F0.imprint","IMPRINT",EDGE,{"derivedFrom":subQ5}),1.0]])]});}
            var Q29;
            Q29=makeQuery(id+"F0.imprint","IMPRINT",FACE,{"disambiguationData":[TD([[makeQuery(id+"F0.imprint","IMPRINT",EDGE,{"derivedFrom":sQuery(id+"F0.wireOp",EDGE,"E496")}),1.0]])]});
            var Q30;
            Q30=makeQuery(id+"F0.imprint","IMPRINT",FACE,{"disambiguationData":[TD([[makeQuery(id+"F0.imprint","IMPRINT",EDGE,{"derivedFrom":sQuery(id+"F0.wireOp",EDGE,"E517")}),-1.0]])]});
            var Q31;
            {var subQ0=sQuery(id+"F0.wireOp",EDGE,"E520");Q31=makeQuery(id+"F0.imprint","IMPRINT",FACE,{"disambiguationData":[TD([[makeQuery(id+"F0.imprint","IMPRINT",EDGE,{"derivedFrom":subQ0}),1.0]])]});}
            var Q32;
            Q32=makeQuery(id+"F0.imprint","IMPRINT",FACE,{"disambiguationData":[TD([[makeQuery(id+"F0.imprint","IMPRINT",EDGE,{"derivedFrom":sQuery(id+"F0.wireOp",EDGE,"E509")}),-1.0]])]});
            var Q33;
            {var subQ4=sQuery(id+"F0.wireOp",EDGE,"E512");Q33=makeQuery(id+"F0.imprint","IMPRINT",FACE,{"disambiguationData":[TD([[makeQuery(id+"F0.imprint","IMPRINT",EDGE,{"derivedFrom":subQ4}),1.0]])]});}
            var Q34;
            {var subQ6=sQuery(id+"F0.wireOp",EDGE,"E548.MirrorCS");Q34=makeQuery(id+"F0.imprint","IMPRINT",FACE,{"disambiguationData":[TD([[makeQuery(id+"F0.imprint","IMPRINT",EDGE,{"derivedFrom":subQ6}),-1.0]])]});}
            var Q35;
            Q35=makeQuery(id+"F0.imprint","IMPRINT",FACE,{"disambiguationData":[TD([[makeQuery(id+"F0.imprint","IMPRINT",EDGE,{"derivedFrom":sQuery(id+"F0.wireOp",EDGE,"E535.MirrorCS")}),-1.0]])]});
            var Q36;
            {var subQ5=sQuery(id+"F0.wireOp",EDGE,"E504");Q36=makeQuery(id+"F0.imprint","IMPRINT",FACE,{"disambiguationData":[TD([[makeQuery(id+"F0.imprint","IMPRINT",EDGE,{"derivedFrom":subQ5}),1.0]])]});}
            var Q37;
            {var subQ5=sQuery(id+"F0.wireOp",EDGE,"E488");Q37=makeQuery(id+"F0.imprint","IMPRINT",FACE,{"disambiguationData":[TD([[makeQuery(id+"F0.imprint","IMPRINT",EDGE,{"derivedFrom":subQ5}),1.0]])]});}
            var Q38;
            {var subQ5=sQuery(id+"F0.wireOp",EDGE,"E540.MirrorCS");Q38=makeQuery(id+"F0.imprint","IMPRINT",FACE,{"disambiguationData":[TD([[makeQuery(id+"F0.imprint","IMPRINT",EDGE,{"derivedFrom":subQ5}),-1.0]])]});}
            var Q39;
            Q39=makeQuery(id+"F0.imprint","IMPRINT",FACE,{"disambiguationData":[TD([[makeQuery(id+"F0.imprint","IMPRINT",EDGE,{"derivedFrom":sQuery(id+"F0.wireOp",EDGE,"E485")}),-1.0]])]});
            var Q40;
            Q40=makeQuery(id+"F0.imprint","IMPRINT",FACE,{"disambiguationData":[TD([[makeQuery(id+"F0.imprint","IMPRINT",EDGE,{"derivedFrom":sQuery(id+"F0.wireOp",EDGE,"E501")}),-1.0]])]});
            extrude(context, id + "F3", {"entities" : qUnion([Q0, Q1, Q2, Q3, Q4, Q5, Q6, Q7, Q8, Q9, Q10, Q11, Q12, Q13, Q14, Q15, Q16, Q17, Q18, Q19, Q20, Q21, Q22, Q23, Q24, Q25, Q26, Q27, Q28, Q29, Q30, Q31, Q32, Q33, Q34, Q35, Q36, Q37, Q38, Q39, Q40]), "depth" : 6.35 * mm});
        }
    });
